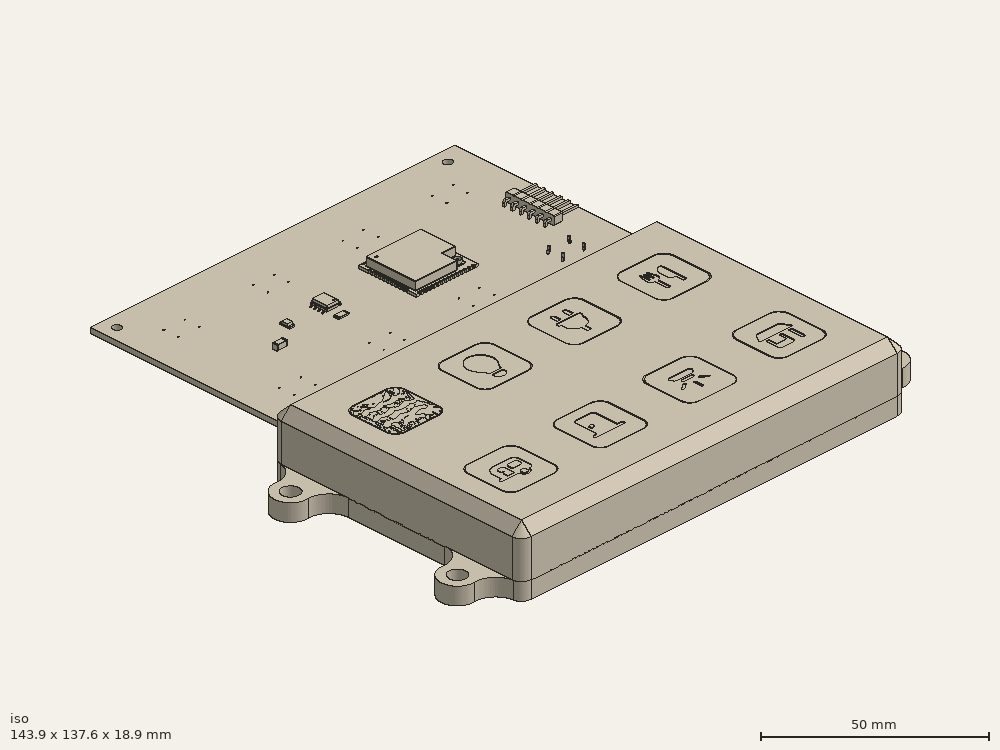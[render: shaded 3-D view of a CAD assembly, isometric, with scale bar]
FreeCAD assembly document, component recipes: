
FREECAD ASSEMBLY — COMPONENT RECIPES ("trailer-switch-panel-eight-buttons")

This assembly document has 11 components, labeled P0..P10 below (a component is one placed body or linked part). 10 of them carry a construction recipe — the FreeCAD feature program that regenerates the part from scratch, quoted from this document or its linked companion documents; the rest are supplied as boundary geometry only. No exploded tour is included for this assembly.
COMPONENT P0 — recipe-attached ("BodyButtonCap001", modeled in this document).
Construction recipe (the document's own serialized feature program — sketch geometry with constraints, then the solid features built on it; lengths are millimeters unless a unit is written):

FEATURE [Sketcher::SketchObject] Sketch036  label="SketchButtonCapBase"
  ArcFitTolerance = 1e-06
  AttachmentSupport = -> [XY_Plane014]
  ExternalTypes = [0]
  FullyConstrained = true
  MakeInternals = false
  MapMode = 5
  expr: Constraints[19] = <<VarSetButtonDimensions>>.Base_button_radius
  expr: Constraints[20] = <<VarSetButtonDimensions>>.Base_button_height
  expr: Constraints[21] = <<VarSetButtonDimensions>>.Base_button_width
  sketch-geometry (10):
    g0: LineSegment StartX=-5 StartY=-8 StartZ=0 EndX=5 EndY=-8 EndZ=0
    g1: LineSegment StartX=8 StartY=-5 StartZ=0 EndX=8 EndY=5 EndZ=0
    g2: LineSegment StartX=5 StartY=8 StartZ=0 EndX=-5 EndY=8 EndZ=0
    g3: LineSegment StartX=-8 StartY=5 StartZ=0 EndX=-8 EndY=-5 EndZ=0
    g4: ArcOfCircle CenterX=-5 CenterY=-5 CenterZ=0 NormalX=0 NormalY=0 NormalZ=1 AngleXU=0 Radius=3 StartAngle=3.14159 EndAngle=4.71239
    g5: ArcOfCircle CenterX=5 CenterY=-5 CenterZ=0 NormalX=0 NormalY=0 NormalZ=1 AngleXU=0 Radius=3 StartAngle=4.71239 EndAngle=6.28319
    g6: ArcOfCircle CenterX=5 CenterY=5 CenterZ=0 NormalX=0 NormalY=0 NormalZ=1 AngleXU=0 Radius=3 StartAngle=1e-16 EndAngle=1.5708
    g7: ArcOfCircle CenterX=-5 CenterY=5 CenterZ=0 NormalX=0 NormalY=0 NormalZ=1 AngleXU=0 Radius=3 StartAngle=1.5708 EndAngle=3.14159
    g8: GeomPoint [constr] X=8 Y=8 Z=0
    g9: GeomPoint [constr] X=0 Y=0 Z=0
  constraints (22):
    c: Tangent(g0,g4) = -1.5708
    c: Tangent(g0,g5) = -1.5708
    c: Tangent(g1,g5) = -1.5708
    c: Tangent(g1,g6) = -1.5708
    c: Tangent(g2,g6) = -1.5708
    c: Tangent(g2,g7) = -1.5708
    c: Tangent(g3,g7) = -1.5708
    c: Tangent(g3,g4) = -1.5708
    c: Horizontal(g0)
    c: Horizontal(g2)
    c: Vertical(g1)
    c: Vertical(g3)
    c: Equal(g4,g5)
    c: Equal(g5,g6)
    c: Equal(g6,g7)
    c: Symmetric(g2,g0,g9)
    c: PointOnObject(g8,g1)
    c: PointOnObject(g8,g2)
    c: Coincident(g9,g-1)
    c: Radius(g5) = 3
    c: DistanceY(g0,g2) = 16
    c: DistanceX(g3,g1) = 16
FEATURE [PartDesign::Plane] DatumPlane004
  AttachmentSupport = -> [Sketch036]
  Length = 60
  MapMode = 7
  Placement = pos=(8,-5,0) rot=(1,0,0;1.5708rad)
  ResizeMode = 0
  Width = 60
FEATURE [PartDesign::Pad] Pad026  label="PadButtonCapPlusBase"
  Direction = (0,0,1)
  Length = 4.59
  Length2 = 10
  Profile = -> Sketch036
  ReferenceAxis = -> Sketch036 [N_Axis]
  Refine = true
  SideType = 0
  Suppressed = false
  Type = 0
  Type2 = 0
  expr: Length = <<VarSetButtonDimensions>>.button_cap_height + <<VarSetButtonDimensions>>.Base_button_slide_depth + <<VarSetButtonDimensions>>.Base_base_thickness
FEATURE [PartDesign::Thickness] Thickness001  label="ThicknessCapWall"
  Base = -> Pad026 [Face9]
  BaseFeature = -> Pad026
  Intersection = false
  Join = 0
  Mode = 0
  Refine = true
  Reversed = true
  SupportTransform = false
  Suppressed = false
  Value = 1.5
  expr: Value = <<VarSetButtonDimensions>>.button_cap_wall_thickness
FEATURE [Sketcher::SketchObject] Sketch050  label="SketchButtonSkirt"
  ArcFitTolerance = 1e-06
  AttachmentSupport = -> [YZ_Plane014]
  ExternalGeometry = -> [Thickness001]
  ExternalTypes = [0]
  FullyConstrained = true
  MakeInternals = false
  MapMode = 5
  Placement = pos=(0,0,0) rot=(0.57735,0.57735,0.57735;2.0944rad)
  sketch-geometry (4):
    g0: LineSegment StartX=8 StartY=0 StartZ=0 EndX=8 EndY=2.5 EndZ=0
    g1: LineSegment StartX=8 StartY=2.5 StartZ=0 EndX=9 EndY=2.5 EndZ=0
    g2: LineSegment StartX=8 StartY=0 StartZ=0 EndX=9 EndY=0 EndZ=0
    g3: LineSegment StartX=9 StartY=2.5 StartZ=0 EndX=9 EndY=0 EndZ=0
  constraints (11):
    c: Coincident(g0,g-3)
    c: PointOnObject(g0,g-3)
    c: DistanceY(g0,g0) = 2.5
    c: Coincident(g1,g0)
    c: Horizontal(g1)
    c: Coincident(g2,g0)
    c: PointOnObject(g2,g-1)
    c: Coincident(g3,g1)
    c: Coincident(g3,g2)
    c: Vertical(g3)
    c: DistanceX(g1,g1) = 1
FEATURE [PartDesign::AdditivePipe] AdditivePipe  label="AdditivePipeButtonSkirt"
  AuxiliaryCurvilinear = true
  AuxiliarySpineTangent = false
  BaseFeature = -> Thickness001
  Binormal = (0,0,0)
  Mode = 0
  Profile = -> Sketch050
  Refine = true
  Spine = -> Thickness001 [Edge15,Edge18,Edge21,Edge23,Edge3,Edge6,Edge9,Edge12]
  SpineTangent = false
  Suppressed = false
  Transformation = 0
  Transition = 0
FEATURE [PartDesign::Pad] Pad035  label="PadButtonBottomContact"
  BaseFeature = -> AdditivePipe
  Direction = (0,0,-1)
  Length = 10
  Length2 = 10
  Profile = -> AdditivePipe [Face28]
  Refine = true
  SideType = 0
  Suppressed = false
  Type = 3
  Type2 = 0
  UpToFace = -> AdditivePipe [Face19]
FEATURE [PartDesign::Pocket] Pocket011  label="PocketBaseShorten"
  BaseFeature = -> Pad035
  Direction = (0,0,1)
  Length = 0.2
  Length2 = 5
  Profile = -> Pad035 [Face19]
  Refine = true
  SideType = 0
  Suppressed = false
  Type = 0
  Type2 = 0
FEATURE [PartDesign::Body] Body004  label="BodyButtonCapBlank"
  AllowCompound = false
  Group = -> [Sketch036,DatumPlane004,Pad026,Thickness001,Sketch050,AdditivePipe,Pad035,Pocket011]
  Origin = -> Origin014
  Placement = pos=(14.41,-15.25,1.6) rot=(0,0,1;0rad)
  Tip = -> Pocket011
COMPONENT P1 — same part as P0; its construction recipe is shown at P0.
COMPONENT P2 — same part as P0; its construction recipe is shown at P0.
COMPONENT P3 — same part as P0; its construction recipe is shown at P0.
COMPONENT P4 — same part as P0; its construction recipe is shown at P0.
COMPONENT P5 — same part as P0; its construction recipe is shown at P0.
COMPONENT P6 — same part as P0; its construction recipe is shown at P0.
COMPONENT P7 — same part as P0; its construction recipe is shown at P0.
COMPONENT P8 — recipe-attached ("BodyCaseBack001", modeled in this document).
Construction recipe (the document's own serialized feature program — sketch geometry with constraints, then the solid features built on it; lengths are millimeters unless a unit is written):

FEATURE [PartDesign::SubShapeBinder] Binder
  BindCopyOnChange = 0
  BindMode = 0
  ClaimChildren = false
  Context = -> Body [Binder.]
  Fuse = false
  MakeFace = true
  OffsetFill = false
  OffsetIntersection = false
  OffsetJoinType = 0
  OffsetOpenResult = false
  PartialLoad = false
  Refine = true
  Relative = true
  Support = -> [Body003[Pocket009.]]
  _Version = 2
FEATURE [Sketcher::SketchObject] Sketch  label="SketchBackOutline"
  ArcFitTolerance = 1e-06
  AttachmentSupport = -> [XY_Plane021]
  ExternalGeometry = -> [Binder]
  ExternalTypes = [0]
  FullyConstrained = true
  MakeInternals = false
  MapMode = 5
  sketch-geometry (8):
    g0: LineSegment StartX=116.87 StartY=6 StartZ=0 EndX=-3 EndY=6 EndZ=0
    g1: LineSegment StartX=-3 StartY=6 StartZ=0 EndX=-3 EndY=-71.81 EndZ=0
    g2: LineSegment StartX=-3 StartY=-71.81 StartZ=0 EndX=116.87 EndY=-71.81 EndZ=0
    g3: LineSegment StartX=116.87 StartY=-71.81 StartZ=0 EndX=116.87 EndY=6 EndZ=0
    g4: Circle CenterX=0 CenterY=-68.81 CenterZ=0 NormalX=0 NormalY=0 NormalZ=1 AngleXU=0 Radius=1.45
    g5: Circle CenterX=113.57 CenterY=-68.81 CenterZ=0 NormalX=0 NormalY=0 NormalZ=1 AngleXU=0 Radius=1.45
    g6: Circle CenterX=113.57 CenterY=2.7 CenterZ=0 NormalX=0 NormalY=0 NormalZ=1 AngleXU=0 Radius=1.45
    g7: Circle CenterX=0 CenterY=2.7 CenterZ=0 NormalX=0 NormalY=0 NormalZ=1 AngleXU=0 Radius=1.45
  constraints (18):
    c: Coincident(g0,g1)
    c: Coincident(g1,g2)
    c: Coincident(g2,g3)
    c: Coincident(g3,g0)
    c: Horizontal(g0)
    c: Horizontal(g2)
    c: Vertical(g1)
    c: Vertical(g3)
    c: Coincident(g0,g-4)
    c: Coincident(g1,g-6)
    c: Coincident(g5,g-7)
    c: Coincident(g6,g-8)
    c: Diameter(g4) = 2.9
    c: Equal(g4,g5)
    c: Coincident(g4,g-9)
    c: Coincident(g7,g-10)
    c: Equal(g7,g4)
    c: Equal(g4,g6)
FEATURE [PartDesign::Pad] Pad  label="PadCaseThickness"
  Direction = (0,0,1)
  Length = 5
  Length2 = 10
  Profile = -> Sketch
  ReferenceAxis = -> Sketch [N_Axis]
  Refine = true
  SideType = 0
  Suppressed = false
  Type = 0
  Type2 = 0
FEATURE [Sketcher::SketchObject] Sketch045  label="SketchMountingTabs"
  ArcFitTolerance = 1e-06
  AttachmentSupport = -> [Pad]
  ExternalGeometry = -> [Pad]
  ExternalTypes = [0]
  FullyConstrained = true
  MakeInternals = false
  MapMode = 5
  Placement = pos=(0,0,0) rot=(1,0,0;3.14159rad)
  sketch-geometry (24):
    g0: Circle CenterX=123.87 CenterY=58.84 CenterZ=0 NormalX=0 NormalY=0 NormalZ=1 AngleXU=0 Radius=2.5
    g1: Circle CenterX=-10 CenterY=58.84 CenterZ=0 NormalX=0 NormalY=0 NormalZ=1 AngleXU=0 Radius=2.5
    g2: Circle CenterX=-10 CenterY=6.97 CenterZ=0 NormalX=0 NormalY=0 NormalZ=1 AngleXU=0 Radius=2.5
    g3: Circle CenterX=123.87 CenterY=6.97 CenterZ=0 NormalX=0 NormalY=0 NormalZ=1 AngleXU=0 Radius=2.5
    g4: GeomPoint X=-3 Y=32.905 Z=0
    g5: GeomPoint X=116.87 Y=32.905 Z=0
    g6: GeomPoint X=-10 Y=32.905 Z=0
    g7: GeomPoint X=123.87 Y=32.905 Z=0
    g8: ArcOfCircle CenterX=-10 CenterY=58.84 CenterZ=0 NormalX=0 NormalY=0 NormalZ=1 AngleXU=0 Radius=5 StartAngle=1.48389 EndAngle=4.79929
    g9: ArcOfCircle CenterX=-10 CenterY=6.97 CenterZ=0 NormalX=0 NormalY=0 NormalZ=1 AngleXU=0 Radius=5 StartAngle=1.48389 EndAngle=4.79929
    g10: ArcOfCircle CenterX=123.87 CenterY=6.97 CenterZ=0 NormalX=0 NormalY=0 NormalZ=1 AngleXU=0 Radius=5 StartAngle=4.62549 EndAngle=7.94088
    g11: ArcOfCircle CenterX=123.87 CenterY=58.84 CenterZ=0 NormalX=0 NormalY=0 NormalZ=1 AngleXU=0 Radius=5 StartAngle=4.62549 EndAngle=7.94088
    g12: ArcOfCircle CenterX=122.912 CenterY=47.84 CenterZ=0 NormalX=0 NormalY=0 NormalZ=1 AngleXU=0 Radius=6.04167 StartAngle=1.48389 EndAngle=3.14159
    g13: ArcOfCircle CenterX=122.912 CenterY=69.84 CenterZ=0 NormalX=0 NormalY=0 NormalZ=1 AngleXU=0 Radius=6.04167 StartAngle=3.14159 EndAngle=4.79929
    g14: ArcOfCircle CenterX=122.912 CenterY=17.97 CenterZ=0 NormalX=0 NormalY=0 NormalZ=1 AngleXU=0 Radius=6.04167 StartAngle=3.14159 EndAngle=4.79929
    g15: ArcOfCircle CenterX=122.912 CenterY=-4.03 CenterZ=0 NormalX=0 NormalY=0 NormalZ=1 AngleXU=0 Radius=6.04167 StartAngle=1.48389 EndAngle=3.14159
    g16: ArcOfCircle CenterX=-9.04167 CenterY=-4.03 CenterZ=0 NormalX=0 NormalY=0 NormalZ=1 AngleXU=0 Radius=6.04167 StartAngle=0 EndAngle=1.6577
    g17: ArcOfCircle CenterX=-9.04167 CenterY=17.97 CenterZ=0 NormalX=0 NormalY=0 NormalZ=1 AngleXU=0 Radius=6.04167 StartAngle=4.62549 EndAngle=6.28319
    g18: ArcOfCircle CenterX=-9.04167 CenterY=47.84 CenterZ=0 NormalX=0 NormalY=0 NormalZ=1 AngleXU=0 Radius=6.04167 StartAngle=0 EndAngle=1.6577
    g19: ArcOfCircle CenterX=-9.04167 CenterY=69.84 CenterZ=0 NormalX=0 NormalY=0 NormalZ=1 AngleXU=0 Radius=6.04167 StartAngle=4.62549 EndAngle=6.28319
    g20: LineSegment StartX=-3 StartY=69.84 StartZ=0 EndX=-3 EndY=47.84 EndZ=0
    g21: LineSegment StartX=-3 StartY=17.97 StartZ=0 EndX=-3 EndY=-4.03 EndZ=0
    g22: LineSegment StartX=116.87 StartY=17.97 StartZ=0 EndX=116.87 EndY=-4.03 EndZ=0
    g23: LineSegment StartX=116.87 StartY=69.84 StartZ=0 EndX=116.87 EndY=47.84 EndZ=0
  constraints (58):
    c: Distance(g0,g-6) = 7
    c: Diameter(g0) = 5
    c: Equal(g0,g2)
    c: Equal(g2,g1)
    c: Horizontal(g1,g0)
    c: Equal(g0,g3)
    c: Vertical(g0,g3)
    c: Symmetric(g-5,g-5,g4)
    c: Symmetric(g-6,g-6,g5)
    c: Symmetric(g0,g3,g7)
    c: Symmetric(g1,g2,g6)
    c: Horizontal(g6,g4)
    c: Horizontal(g5,g7)
    c: Vertical(g2,g1)
    c: DistanceX(g1,g-5) = 7
    c: DistanceY(g-5,g-5) = 77.81
    c: DistanceY(g1,g-5) = 12.97
    c: PointOnObject(g15,g-6)
    c: PointOnObject(g16,g-5)
    c: Tangent(g19,g-5) = -1.5708
    c: Tangent(g19,g8) = 1.5708
    c: Tangent(g18,g8) = 1.5708
    c: Coincident(g8,g1)
    c: Vertical(g8,g8)
    c: DistanceY(g18,g19) = 22
    c: Radius(g8) = 5
    c: Tangent(g17,g-5) = -1.5708
    c: Tangent(g17,g9) = 1.5708
    c: Tangent(g16,g9) = 1.5708
    c: Equal(g9,g8)
    c: Coincident(g9,g2)
    c: DistanceY(g16,g17) = 22
    c: Vertical(g9,g9)
    c: Vertical(g9,g8)
    c: Tangent(g13,g-6) = -1.5708
    c: Tangent(g13,g11) = 1.5708
    c: Tangent(g12,g11) = 1.5708
    c: Tangent(g12,g-6) = -1.5708
    c: Coincident(g11,g0)
    c: Vertical(g11,g11)
    c: Equal(g8,g11)
    c: Horizontal(g13,g19)
    c: Tangent(g14,g-6) = -1.5708
    c: Tangent(g14,g10) = 1.5708
    c: Tangent(g15,g10) = 1.5708
    c: Vertical(g10,g10)
    c: Vertical(g10,g11)
    c: Coincident(g10,g3)
    c: Tangent(g-6,g15,g15) = -1.5708
    c: Horizontal(g14,g17)
    c: Tangent(g20,g19) = 1.5708
    c: Coincident(g20,g18)
    c: Coincident(g21,g17)
    c: Tangent(g21,g16) = 1.5708
    c: Coincident(g22,g14)
    c: Coincident(g22,g15)
    c: Coincident(g23,g13)
    c: Coincident(g23,g12)
FEATURE [PartDesign::Pad] Pad032  label="PadMountingTabs"
  BaseFeature = -> Pad
  Direction = (0,0,-1)
  Length = 5
  Length2 = 10
  Profile = -> Sketch045
  ReferenceAxis = -> Sketch045 [N_Axis]
  Refine = true
  Reversed = true
  SideType = 0
  Suppressed = false
  Type = 0
  Type2 = 0
FEATURE [Sketcher::SketchObject] Sketch046
  ArcFitTolerance = 1e-06
  AttachmentSupport = -> [Pad032]
  ExternalGeometry = -> [Pad032]
  ExternalTypes = [0]
  FullyConstrained = true
  MakeInternals = false
  MapMode = 5
  Placement = pos=(0,0,0) rot=(1,0,0;3.14159rad)
  sketch-geometry (4):
    g0: Circle CenterX=0 CenterY=-2.7 CenterZ=0 NormalX=0 NormalY=0 NormalZ=1 AngleXU=0 Radius=2.3
    g1: Circle CenterX=113.57 CenterY=-2.7 CenterZ=0 NormalX=0 NormalY=0 NormalZ=1 AngleXU=0 Radius=2.3
    g2: Circle CenterX=113.57 CenterY=68.81 CenterZ=0 NormalX=0 NormalY=0 NormalZ=1 AngleXU=0 Radius=2.3
    g3: Circle CenterX=0 CenterY=68.81 CenterZ=0 NormalX=0 NormalY=0 NormalZ=1 AngleXU=0 Radius=2.3
  constraints (8):
    c: Coincident(g1,g-4)
    c: Coincident(g2,g-3)
    c: Diameter(g3) = 4.6
    c: Equal(g3,g2)
    c: Equal(g2,g1)
    c: Equal(g1,g0)
    c: Coincident(g3,g-5)
    c: Coincident(g-6,g0)
FEATURE [PartDesign::Pocket] Pocket
  BaseFeature = -> Pad032
  Direction = (0,0,1)
  Length = 3.5
  Length2 = 5
  Profile = -> Sketch046
  ReferenceAxis = -> Sketch046 [N_Axis]
  Refine = true
  SideType = 0
  Suppressed = false
  Type = 0
  Type2 = 0
FEATURE [Sketcher::SketchObject] Sketch051
  ArcFitTolerance = 1e-06
  AttachmentSupport = -> [Pocket]
  ExternalGeometry = -> [Pocket]
  ExternalTypes = [0]
  FullyConstrained = true
  MakeInternals = false
  MapMode = 5
  Placement = pos=(0,0,5) rot=(0,0,1;0rad)
  sketch-geometry (6):
    g0: GeomPoint X=56.935 Y=-32.905 Z=0
    g1: LineSegment StartX=7 StartY=1 StartZ=0 EndX=7 EndY=-66.81 EndZ=0
    g2: LineSegment StartX=7 StartY=-66.81 StartZ=0 EndX=106.87 EndY=-66.81 EndZ=0
    g3: LineSegment StartX=106.87 StartY=-66.81 StartZ=0 EndX=106.87 EndY=1 EndZ=0
    g4: LineSegment StartX=106.87 StartY=1 StartZ=0 EndX=7 EndY=1 EndZ=0
    g5: GeomPoint [constr] X=56.935 Y=-32.905 Z=0
  constraints (13):
    c: Symmetric(g-3,g-4,g0)
    c: Coincident(g1,g2)
    c: Coincident(g2,g3)
    c: Coincident(g3,g4)
    c: Coincident(g4,g1)
    c: Vertical(g1)
    c: Vertical(g3)
    c: Horizontal(g2)
    c: Horizontal(g4)
    c: Symmetric(g3,g1,g5)
    c: Coincident(g5,g0)
    c: DistanceY(g1,g-3) = 5
    c: DistanceX(g-3,g1) = 10
FEATURE [PartDesign::Pocket] Pocket012
  BaseFeature = -> Pocket
  Direction = (0,0,-1)
  Length = 2
  Length2 = 5
  Profile = -> Sketch051
  ReferenceAxis = -> Sketch051 [N_Axis]
  Refine = true
  SideType = 0
  Suppressed = false
  Type = 0
  Type2 = 0
FEATURE [PartDesign::Fillet] Fillet001
  Base = -> Pocket012 [Edge32,Edge2,Edge66,Edge65]
  BaseFeature = -> Pocket012
  Radius = 3
  Refine = true
  SupportTransform = false
  Suppressed = false
  UseAllEdges = false
FEATURE [PartDesign::Body] Body  label="BodyCaseBack"
  AllowCompound = false
  Group = -> [Binder,Sketch,Pad,Sketch045,Pad032,Sketch046,Pocket,Sketch051,Pocket012,Fillet001]
  Origin = -> Origin021
  Placement = pos=(0,0,-12.73) rot=(0,0,1;0rad)
  Tip = -> Fillet001
COMPONENT P9 — recipe-attached ("BodyFrontMountPcbButtonCover001", modeled in this document).
Construction recipe (the document's own serialized feature program — sketch geometry with constraints, then the solid features built on it; lengths are millimeters unless a unit is written):

FEATURE [PartDesign::SubShapeBinder] Binder006  label="BinderPcb001"
  BindCopyOnChange = 0
  BindMode = 0
  ClaimChildren = false
  Context = -> Body003 [Binder006.]
  Fuse = false
  MakeFace = true
  OffsetFill = false
  OffsetIntersection = false
  OffsetJoinType = 0
  OffsetOpenResult = false
  PartialLoad = false
  Placement = pos=(0,0,-3.64) rot=(0,0,1;0rad)
  Refine = true
  Relative = true
  Support = -> [Board_cc27]
  _Version = 2
FEATURE [Sketcher::SketchObject] Sketch033  label="SketchBackPlateToCover"
  ArcFitTolerance = 1e-06
  AttachmentSupport = -> [XY_Plane013]
  ExternalGeometry = -> [Binder006]
  ExternalTypes = [0]
  FullyConstrained = true
  MakeInternals = false
  MapMode = 5
  expr: Constraints[19] = <<VarSetButtonDimensions>>.Base_button_width + <<VarSetButtonDimensions>>.tolerance
  expr: Constraints[20] = <<VarSetButtonDimensions>>.Base_button_height + <<VarSetButtonDimensions>>.tolerance
  expr: Constraints[33] = <<VarSetButtonDimensions>>.Base_button_radius
  sketch-geometry (84):
    g0: LineSegment StartX=6.2 StartY=-10.05 StartZ=0 EndX=6.2 EndY=-20.45 EndZ=0
    g1: LineSegment StartX=9.2 StartY=-23.45 StartZ=0 EndX=19.6 EndY=-23.45 EndZ=0
    g2: LineSegment StartX=22.6 StartY=-20.45 StartZ=0 EndX=22.6 EndY=-10.05 EndZ=0
    g3: LineSegment StartX=19.6 StartY=-7.05 StartZ=0 EndX=9.2 EndY=-7.05 EndZ=0
    g4: ArcOfCircle CenterX=9.2 CenterY=-10.05 CenterZ=0 NormalX=0 NormalY=0 NormalZ=1 AngleXU=0 Radius=3 StartAngle=1.5708 EndAngle=3.14159
    g5: ArcOfCircle CenterX=9.2 CenterY=-20.45 CenterZ=0 NormalX=0 NormalY=0 NormalZ=1 AngleXU=0 Radius=3 StartAngle=3.14159 EndAngle=4.71239
    g6: ArcOfCircle CenterX=19.6 CenterY=-20.45 CenterZ=0 NormalX=0 NormalY=0 NormalZ=1 AngleXU=0 Radius=3 StartAngle=4.71239 EndAngle=6.28319
    g7: ArcOfCircle CenterX=19.6 CenterY=-10.05 CenterZ=0 NormalX=0 NormalY=0 NormalZ=1 AngleXU=0 Radius=3 StartAngle=6e-16 EndAngle=1.5708
    g8: GeomPoint [constr] X=6.2 Y=-7.05 Z=0
    g9: GeomPoint [constr] X=22.6 Y=-23.45 Z=0
    g10: LineSegment StartX=-3 StartY=6 StartZ=0 EndX=-3 EndY=-71.81 EndZ=0
    g11: LineSegment StartX=-3 StartY=-71.81 StartZ=0 EndX=116.87 EndY=-71.81 EndZ=0
    g12: LineSegment StartX=116.87 StartY=-71.81 StartZ=0 EndX=116.87 EndY=6 EndZ=0
    g13: LineSegment StartX=116.87 StartY=6 StartZ=0 EndX=-3 EndY=6 EndZ=0
    g14: LineSegment StartX=34.04 StartY=-10.05 StartZ=0 EndX=34.04 EndY=-20.45 EndZ=0
    g15: LineSegment StartX=37.04 StartY=-23.45 StartZ=0 EndX=47.44 EndY=-23.45 EndZ=0
    g16: LineSegment StartX=50.44 StartY=-20.45 StartZ=0 EndX=50.44 EndY=-10.05 EndZ=0
    g17: LineSegment StartX=47.44 StartY=-7.05 StartZ=0 EndX=37.04 EndY=-7.05 EndZ=0
    g18: ArcOfCircle CenterX=37.04 CenterY=-10.05 CenterZ=0 NormalX=0 NormalY=0 NormalZ=1 AngleXU=0 Radius=3 StartAngle=1.5708 EndAngle=3.14159
    g19: ArcOfCircle CenterX=37.04 CenterY=-20.45 CenterZ=0 NormalX=0 NormalY=0 NormalZ=1 AngleXU=0 Radius=3 StartAngle=3.14159 EndAngle=4.71239
    g20: ArcOfCircle CenterX=47.44 CenterY=-20.45 CenterZ=0 NormalX=0 NormalY=0 NormalZ=1 AngleXU=0 Radius=3 StartAngle=4.71239 EndAngle=6.28319
    g21: ArcOfCircle CenterX=47.44 CenterY=-10.05 CenterZ=0 NormalX=0 NormalY=0 NormalZ=1 AngleXU=0 Radius=3 StartAngle=0 EndAngle=1.5708
    g22: GeomPoint [constr] X=50.44 Y=-23.45 Z=0
    g23: GeomPoint [constr] X=42.24 Y=-15.25 Z=0
    g24: LineSegment StartX=61.88 StartY=-10.05 StartZ=0 EndX=61.88 EndY=-20.45 EndZ=0
    g25: LineSegment StartX=64.88 StartY=-23.45 StartZ=0 EndX=75.28 EndY=-23.45 EndZ=0
    g26: LineSegment StartX=78.28 StartY=-20.45 StartZ=0 EndX=78.28 EndY=-10.05 EndZ=0
    g27: LineSegment StartX=75.28 StartY=-7.05 StartZ=0 EndX=64.88 EndY=-7.05 EndZ=0
    g28: ArcOfCircle CenterX=64.88 CenterY=-10.05 CenterZ=0 NormalX=0 NormalY=0 NormalZ=1 AngleXU=0 Radius=3 StartAngle=1.5708 EndAngle=3.14159
    g29: ArcOfCircle CenterX=64.88 CenterY=-20.45 CenterZ=0 NormalX=0 NormalY=0 NormalZ=1 AngleXU=0 Radius=3 StartAngle=3.14159 EndAngle=4.71239
    g30: ArcOfCircle CenterX=75.28 CenterY=-20.45 CenterZ=0 NormalX=0 NormalY=0 NormalZ=1 AngleXU=0 Radius=3 StartAngle=4.71239 EndAngle=6.28319
    g31: ArcOfCircle CenterX=75.28 CenterY=-10.05 CenterZ=0 NormalX=0 NormalY=0 NormalZ=1 AngleXU=0 Radius=3 StartAngle=1e-16 EndAngle=1.5708
    g32: GeomPoint [constr] X=78.28 Y=-23.45 Z=0
    g33: GeomPoint [constr] X=70.08 Y=-15.25 Z=0
    g34: LineSegment StartX=89.72 StartY=-10.05 StartZ=0 EndX=89.72 EndY=-20.45 EndZ=0
    g35: LineSegment StartX=92.72 StartY=-23.45 StartZ=0 EndX=103.12 EndY=-23.45 EndZ=0
    g36: LineSegment StartX=106.12 StartY=-20.45 StartZ=0 EndX=106.12 EndY=-10.05 EndZ=0
    g37: LineSegment StartX=103.12 StartY=-7.05 StartZ=0 EndX=92.72 EndY=-7.05 EndZ=0
    g38: ArcOfCircle CenterX=92.72 CenterY=-10.05 CenterZ=0 NormalX=0 NormalY=0 NormalZ=1 AngleXU=0 Radius=3 StartAngle=1.5708 EndAngle=3.14159
    g39: ArcOfCircle CenterX=92.72 CenterY=-20.45 CenterZ=0 NormalX=0 NormalY=0 NormalZ=1 AngleXU=0 Radius=3 StartAngle=3.14159 EndAngle=4.71239
    g40: ArcOfCircle CenterX=103.12 CenterY=-20.45 CenterZ=0 NormalX=0 NormalY=0 NormalZ=1 AngleXU=0 Radius=3 StartAngle=4.71239 EndAngle=6.28319
    g41: ArcOfCircle CenterX=103.12 CenterY=-10.05 CenterZ=0 NormalX=0 NormalY=0 NormalZ=1 AngleXU=0 Radius=3 StartAngle=3e-16 EndAngle=1.5708
    g42: GeomPoint [constr] X=106.12 Y=-23.45 Z=0
    g43: GeomPoint [constr] X=97.92 Y=-15.25 Z=0
    g44: LineSegment StartX=6 StartY=-46.08 StartZ=0 EndX=6 EndY=-56.48 EndZ=0
    g45: LineSegment StartX=9 StartY=-59.48 StartZ=0 EndX=19.4 EndY=-59.48 EndZ=0
    g46: LineSegment StartX=22.4 StartY=-56.48 StartZ=0 EndX=22.4 EndY=-46.08 EndZ=0
    g47: LineSegment StartX=19.4 StartY=-43.08 StartZ=0 EndX=9 EndY=-43.08 EndZ=0
    g48: ArcOfCircle CenterX=9 CenterY=-46.08 CenterZ=0 NormalX=0 NormalY=0 NormalZ=1 AngleXU=0 Radius=3 StartAngle=1.5708 EndAngle=3.14159
    g49: ArcOfCircle CenterX=9 CenterY=-56.48 CenterZ=0 NormalX=0 NormalY=0 NormalZ=1 AngleXU=0 Radius=3 StartAngle=3.14159 EndAngle=4.71239
    g50: ArcOfCircle CenterX=19.4 CenterY=-56.48 CenterZ=0 NormalX=0 NormalY=0 NormalZ=1 AngleXU=0 Radius=3 StartAngle=4.71239 EndAngle=6.28319
    g51: ArcOfCircle CenterX=19.4 CenterY=-46.08 CenterZ=0 NormalX=0 NormalY=0 NormalZ=1 AngleXU=0 Radius=3 StartAngle=9e-16 EndAngle=1.5708
    g52: GeomPoint [constr] X=22.4 Y=-59.48 Z=0
    g53: GeomPoint [constr] X=14.2 Y=-51.28 Z=0
    g54: LineSegment StartX=33.84 StartY=-46.08 StartZ=0 EndX=33.84 EndY=-56.48 EndZ=0
    g55: LineSegment StartX=36.84 StartY=-59.48 StartZ=0 EndX=47.24 EndY=-59.48 EndZ=0
    g56: LineSegment StartX=50.24 StartY=-56.48 StartZ=0 EndX=50.24 EndY=-46.08 EndZ=0
    g57: LineSegment StartX=47.24 StartY=-43.08 StartZ=0 EndX=36.84 EndY=-43.08 EndZ=0
    g58: ArcOfCircle CenterX=36.84 CenterY=-46.08 CenterZ=0 NormalX=0 NormalY=0 NormalZ=1 AngleXU=0 Radius=3 StartAngle=1.5708 EndAngle=3.14159
    g59: ArcOfCircle CenterX=36.84 CenterY=-56.48 CenterZ=0 NormalX=0 NormalY=0 NormalZ=1 AngleXU=0 Radius=3 StartAngle=3.14159 EndAngle=4.71239
    g60: ArcOfCircle CenterX=47.24 CenterY=-56.48 CenterZ=0 NormalX=0 NormalY=0 NormalZ=1 AngleXU=0 Radius=3 StartAngle=4.71239 EndAngle=6.28319
    g61: ArcOfCircle CenterX=47.24 CenterY=-46.08 CenterZ=0 NormalX=0 NormalY=0 NormalZ=1 AngleXU=0 Radius=3 StartAngle=7e-16 EndAngle=1.5708
    g62: GeomPoint [constr] X=50.24 Y=-59.48 Z=0
    g63: GeomPoint [constr] X=42.04 Y=-51.28 Z=0
    g64: LineSegment StartX=61.68 StartY=-46.08 StartZ=0 EndX=61.68 EndY=-56.48 EndZ=0
    g65: LineSegment StartX=64.68 StartY=-59.48 StartZ=0 EndX=75.08 EndY=-59.48 EndZ=0
    g66: LineSegment StartX=78.08 StartY=-56.48 StartZ=0 EndX=78.08 EndY=-46.08 EndZ=0
    g67: LineSegment StartX=75.08 StartY=-43.08 StartZ=0 EndX=64.68 EndY=-43.08 EndZ=0
    g68: ArcOfCircle CenterX=64.68 CenterY=-46.08 CenterZ=0 NormalX=0 NormalY=0 NormalZ=1 AngleXU=0 Radius=3 StartAngle=1.5708 EndAngle=3.14159
    g69: ArcOfCircle CenterX=64.68 CenterY=-56.48 CenterZ=0 NormalX=0 NormalY=0 NormalZ=1 AngleXU=0 Radius=3 StartAngle=3.14159 EndAngle=4.71239
    g70: ArcOfCircle CenterX=75.08 CenterY=-56.48 CenterZ=0 NormalX=0 NormalY=0 NormalZ=1 AngleXU=0 Radius=3 StartAngle=4.71239 EndAngle=6.28319
    g71: ArcOfCircle CenterX=75.08 CenterY=-46.08 CenterZ=0 NormalX=0 NormalY=0 NormalZ=1 AngleXU=0 Radius=3 StartAngle=9e-16 EndAngle=1.5708
    g72: GeomPoint [constr] X=78.08 Y=-59.48 Z=0
    g73: GeomPoint [constr] X=69.88 Y=-51.28 Z=0
    g74: LineSegment StartX=89.52 StartY=-46.08 StartZ=0 EndX=89.52 EndY=-56.48 EndZ=0
    g75: LineSegment StartX=92.52 StartY=-59.48 StartZ=0 EndX=102.92 EndY=-59.48 EndZ=0
    g76: LineSegment StartX=105.92 StartY=-56.48 StartZ=0 EndX=105.92 EndY=-46.08 EndZ=0
    g77: LineSegment StartX=102.92 StartY=-43.08 StartZ=0 EndX=92.52 EndY=-43.08 EndZ=0
    g78: ArcOfCircle CenterX=92.52 CenterY=-46.08 CenterZ=0 NormalX=0 NormalY=0 NormalZ=1 AngleXU=0 Radius=3 StartAngle=1.5708 EndAngle=3.14159
    g79: ArcOfCircle CenterX=92.52 CenterY=-56.48 CenterZ=0 NormalX=0 NormalY=0 NormalZ=1 AngleXU=0 Radius=3 StartAngle=3.14159 EndAngle=4.71239
    g80: ArcOfCircle CenterX=102.92 CenterY=-56.48 CenterZ=0 NormalX=0 NormalY=0 NormalZ=1 AngleXU=0 Radius=3 StartAngle=4.71239 EndAngle=6.28319
    g81: ArcOfCircle CenterX=102.92 CenterY=-46.08 CenterZ=0 NormalX=0 NormalY=0 NormalZ=1 AngleXU=0 Radius=3 StartAngle=6e-16 EndAngle=1.5708
    g82: GeomPoint [constr] X=105.92 Y=-59.48 Z=0
    g83: GeomPoint [constr] X=97.72 Y=-51.28 Z=0
  constraints (189):
    c: Tangent(g0,g4) = -1.5708
    c: Tangent(g0,g5) = -1.5708
    c: Tangent(g1,g5) = -1.5708
    c: Tangent(g1,g6) = -1.5708
    c: Tangent(g2,g6) = -1.5708
    c: Tangent(g2,g7) = -1.5708
    c: Tangent(g3,g7) = -1.5708
    c: Tangent(g3,g4) = -1.5708
    c: Vertical(g0)
    c: Vertical(g2)
    c: Horizontal(g1)
    c: Horizontal(g3)
    c: Equal(g4,g5)
    c: Equal(g5,g6)
    c: Equal(g6,g7)
    c: PointOnObject(g8,g0)
    c: PointOnObject(g8,g3)
    c: PointOnObject(g9,g1)
    c: PointOnObject(g9,g2)
    c: Distance(g0,g2) = 16.4
    c: Distance(g1,g3) = 16.4
    c: Coincident(g10,g11)
    c: Coincident(g11,g12)
    c: Coincident(g12,g13)
    c: Coincident(g13,g10)
    c: Vertical(g10)
    c: Vertical(g12)
    c: Horizontal(g11)
    c: Horizontal(g13)
    c: DistanceX(g10,g-1) = 3
    c: DistanceY(g-1,g10) = 6
    c: DistanceX(g-5,g11) = 3
    c: DistanceY(g11,g-5) = 6
    c: Radius(g7) = 3
    c: Symmetric(g4,g6,g-7)
    c: Tangent(g14,g18) = -1.5708
    c: Tangent(g14,g19) = -1.5708
    c: Tangent(g15,g19) = -1.5708
    c: Tangent(g15,g20) = -1.5708
    c: Tangent(g16,g20) = -1.5708
    c: Tangent(g16,g21) = -1.5708
    c: Tangent(g17,g21) = -1.5708
    c: Tangent(g17,g18) = -1.5708
    c: Vertical(g14)
    c: Vertical(g16)
    c: Horizontal(g15)
    c: Horizontal(g17)
    c: Equal(g18,g19)
    c: Equal(g19,g20)
    c: Equal(g20,g21)
    c: Symmetric(g16,g14,g23)
    c: PointOnObject(g22,g15)
    c: PointOnObject(g22,g16)
    c: Coincident(g23,g-8)
    c: Tangent(g24,g28) = -1.5708
    c: Tangent(g24,g29) = -1.5708
    c: Tangent(g25,g29) = -1.5708
    c: Tangent(g25,g30) = -1.5708
    c: Tangent(g26,g30) = -1.5708
    c: Tangent(g26,g31) = -1.5708
    c: Tangent(g27,g31) = -1.5708
    c: Tangent(g27,g28) = -1.5708
    c: Vertical(g24)
    c: Vertical(g26)
    c: Horizontal(g25)
    c: Horizontal(g27)
    c: Equal(g28,g29)
    c: Equal(g29,g30)
    c: Equal(g30,g31)
    c: Symmetric(g26,g24,g33)
    c: PointOnObject(g32,g25)
    c: PointOnObject(g32,g26)
    c: Coincident(g33,g-9)
    c: Tangent(g34,g38) = -1.5708
    c: Tangent(g34,g39) = -1.5708
    c: Tangent(g35,g39) = -1.5708
    c: Tangent(g35,g40) = -1.5708
    c: Tangent(g36,g40) = -1.5708
    c: Tangent(g36,g41) = -1.5708
    c: Tangent(g37,g41) = -1.5708
    c: Tangent(g37,g38) = -1.5708
    c: Vertical(g34)
    c: Vertical(g36)
    c: Horizontal(g35)
    c: Horizontal(g37)
    c: Equal(g38,g39)
    c: Equal(g39,g40)
    c: Equal(g40,g41)
    c: Symmetric(g36,g34,g43)
    c: PointOnObject(g42,g35)
    c: PointOnObject(g42,g36)
    c: Coincident(g43,g-10)
    c: Tangent(g44,g48) = -1.5708
    c: Tangent(g44,g49) = -1.5708
    c: Tangent(g45,g49) = -1.5708
    c: Tangent(g45,g50) = -1.5708
    c: Tangent(g46,g50) = -1.5708
    c: Tangent(g46,g51) = -1.5708
    c: Tangent(g47,g51) = -1.5708
    c: Tangent(g47,g48) = -1.5708
    c: Vertical(g44)
    c: Vertical(g46)
    c: Horizontal(g45)
    c: Horizontal(g47)
    c: Equal(g48,g49)
    c: Equal(g49,g50)
    c: Equal(g50,g51)
    c: Symmetric(g46,g44,g53)
    c: PointOnObject(g52,g45)
    c: PointOnObject(g52,g46)
    c: Coincident(g53,g-14)
    c: Tangent(g54,g58) = -1.5708
    c: Tangent(g54,g59) = -1.5708
    c: Tangent(g55,g59) = -1.5708
    c: Tangent(g55,g60) = -1.5708
    c: Tangent(g56,g60) = -1.5708
    c: Tangent(g56,g61) = -1.5708
    c: Tangent(g57,g61) = -1.5708
    c: Tangent(g57,g58) = -1.5708
    c: Vertical(g54)
    c: Vertical(g56)
    c: Horizontal(g55)
    c: Horizontal(g57)
    c: Equal(g58,g59)
    c: Equal(g59,g60)
    c: Equal(g60,g61)
    c: Symmetric(g56,g54,g63)
    c: PointOnObject(g62,g55)
    c: PointOnObject(g62,g56)
    c: Coincident(g63,g-13)
    c: Tangent(g64,g68) = -1.5708
    c: Tangent(g64,g69) = -1.5708
    c: Tangent(g65,g69) = -1.5708
    c: Tangent(g65,g70) = -1.5708
    c: Tangent(g66,g70) = -1.5708
    c: Tangent(g66,g71) = -1.5708
    c: Tangent(g67,g71) = -1.5708
    c: Tangent(g67,g68) = -1.5708
    c: Vertical(g64)
    c: Vertical(g66)
    c: Horizontal(g65)
    c: Horizontal(g67)
    c: Equal(g68,g69)
    c: Equal(g69,g70)
    c: Equal(g70,g71)
    c: Symmetric(g66,g64,g73)
    c: PointOnObject(g72,g65)
    c: PointOnObject(g72,g66)
    c: Coincident(g73,g-12)
    c: Tangent(g74,g78) = -1.5708
    c: Tangent(g74,g79) = -1.5708
    c: Tangent(g75,g79) = -1.5708
    c: Tangent(g75,g80) = -1.5708
    c: Tangent(g76,g80) = -1.5708
    c: Tangent(g76,g81) = -1.5708
    c: Tangent(g77,g81) = -1.5708
    c: Tangent(g77,g78) = -1.5708
    c: Vertical(g74)
    c: Vertical(g76)
    c: Horizontal(g75)
    c: Horizontal(g77)
    c: Equal(g78,g79)
    c: Equal(g79,g80)
    c: Equal(g80,g81)
    c: Symmetric(g76,g74,g83)
    c: PointOnObject(g82,g75)
    c: PointOnObject(g82,g76)
    c: Coincident(g83,g-11)
    c: Equal(g4,g18)
    c: Equal(g18,g48)
    c: Equal(g48,g58)
    c: Equal(g58,g68)
    c: Equal(g68,g28)
    c: Equal(g28,g38)
    c: Equal(g38,g78)
    c: Equal(g2,g16)
    c: Equal(g16,g26)
    c: Equal(g26,g36)
    c: Equal(g36,g76)
    c: Equal(g76,g66)
    c: Equal(g66,g56)
    c: Equal(g56,g46)
    c: Equal(g3,g17)
    c: Equal(g17,g27)
    c: Equal(g27,g37)
    c: Equal(g37,g77)
    c: Equal(g77,g67)
    c: Equal(g67,g57)
    c: Equal(g57,g47)
FEATURE [PartDesign::Pad] Pad024  label="PadOuterWalls"
  Direction = (0,0,1)
  Length = 1.5
  Length2 = 10
  Profile = -> Sketch033
  ReferenceAxis = -> Sketch033 [N_Axis]
  Refine = true
  SideType = 0
  Suppressed = false
  Type = 0
  Type2 = 0
  expr: Length = <<VarSetButtonDimensions>>.Base_base_thickness
FEATURE [Sketcher::SketchObject] Sketch034  label="SketchButtonSlide"
  ArcFitTolerance = 1e-06
  AttachmentSupport = -> [Pad024]
  ExternalGeometry = -> [Pad024]
  ExternalTypes = [0]
  FullyConstrained = true
  MakeInternals = false
  MapMode = 5
  Placement = pos=(0,0,1.5) rot=(0,0,1;0rad)
  expr: Constraints[29] = <<VarSetButtonDimensions>>.Base_button_radius
  expr: Constraints[30] = <<VarSetButtonDimensions>>.Base_button_width + <<VarSetButtonDimensions>>.tolerance + <<VarSetButtonDimensions>>.button_snap_thickness * 2 + <<VarSetButtonDimensions>>.button_tab_depth
  expr: Constraints[31] = <<VarSetButtonDimensions>>.Base_button_width + <<VarSetButtonDimensions>>.tolerance + <<VarSetButtonDimensions>>.button_snap_thickness * 2 + <<VarSetButtonDimensions>>.button_tab_depth
  sketch-geometry (93):
    g0: LineSegment StartX=-3 StartY=6 StartZ=0 EndX=-3 EndY=-71.81 EndZ=0
    g1: LineSegment StartX=-3 StartY=-71.81 StartZ=0 EndX=116.87 EndY=-71.81 EndZ=0
    g2: LineSegment StartX=116.87 StartY=-71.81 StartZ=0 EndX=116.87 EndY=6 EndZ=0
    g3: LineSegment StartX=116.87 StartY=6 StartZ=0 EndX=-3 EndY=6 EndZ=0
    g4: LineSegment StartX=5.2 StartY=-9.05 StartZ=0 EndX=5.2 EndY=-21.45 EndZ=0
    g5: LineSegment StartX=8.2 StartY=-24.45 StartZ=0 EndX=20.6 EndY=-24.45 EndZ=0
    g6: LineSegment StartX=23.6 StartY=-21.45 StartZ=0 EndX=23.6 EndY=-9.05 EndZ=0
    g7: LineSegment StartX=20.6 StartY=-6.05 StartZ=0 EndX=8.2 EndY=-6.05 EndZ=0
    g8: ArcOfCircle CenterX=8.2 CenterY=-9.05 CenterZ=0 NormalX=0 NormalY=0 NormalZ=1 AngleXU=0 Radius=3 StartAngle=1.5708 EndAngle=3.14159
    g9: ArcOfCircle CenterX=8.2 CenterY=-21.45 CenterZ=0 NormalX=0 NormalY=0 NormalZ=1 AngleXU=0 Radius=3 StartAngle=3.14159 EndAngle=4.71239
    g10: ArcOfCircle CenterX=20.6 CenterY=-21.45 CenterZ=0 NormalX=0 NormalY=0 NormalZ=1 AngleXU=0 Radius=3 StartAngle=4.71239 EndAngle=6.28319
    g11: ArcOfCircle CenterX=20.6 CenterY=-9.05 CenterZ=0 NormalX=0 NormalY=0 NormalZ=1 AngleXU=0 Radius=3 StartAngle=0 EndAngle=1.5708
    g12: GeomPoint [constr] X=5.2 Y=-6.05 Z=0
    g13: GeomPoint [constr] X=23.6 Y=-24.45 Z=0
    g14: GeomPoint X=14.4 Y=-15.25 Z=0
    g15: GeomPoint X=14.4 Y=-15.25 Z=0
    g16: LineSegment StartX=33.04 StartY=-9.05 StartZ=0 EndX=33.04 EndY=-21.45 EndZ=0
    g17: LineSegment StartX=36.04 StartY=-24.45 StartZ=0 EndX=48.44 EndY=-24.45 EndZ=0
    g18: LineSegment StartX=51.44 StartY=-21.45 StartZ=0 EndX=51.44 EndY=-9.05 EndZ=0
    g19: LineSegment StartX=48.44 StartY=-6.05 StartZ=0 EndX=36.04 EndY=-6.05 EndZ=0
    g20: ArcOfCircle CenterX=36.04 CenterY=-9.05 CenterZ=0 NormalX=0 NormalY=0 NormalZ=1 AngleXU=0 Radius=3 StartAngle=1.5708 EndAngle=3.14159
    g21: ArcOfCircle CenterX=36.04 CenterY=-21.45 CenterZ=0 NormalX=0 NormalY=0 NormalZ=1 AngleXU=0 Radius=3 StartAngle=3.14159 EndAngle=4.71239
    g22: ArcOfCircle CenterX=48.44 CenterY=-21.45 CenterZ=0 NormalX=0 NormalY=0 NormalZ=1 AngleXU=0 Radius=3 StartAngle=4.71239 EndAngle=6.28319
    g23: ArcOfCircle CenterX=48.44 CenterY=-9.05 CenterZ=0 NormalX=0 NormalY=0 NormalZ=1 AngleXU=0 Radius=3 StartAngle=0 EndAngle=1.5708
    g24: GeomPoint [constr] X=33.04 Y=-6.05 Z=0
    g25: GeomPoint [constr] X=51.44 Y=-24.45 Z=0
    g26: LineSegment StartX=60.88 StartY=-9.05 StartZ=0 EndX=60.88 EndY=-21.45 EndZ=0
    g27: LineSegment StartX=63.88 StartY=-24.45 StartZ=0 EndX=76.28 EndY=-24.45 EndZ=0
    g28: LineSegment StartX=79.28 StartY=-21.45 StartZ=0 EndX=79.28 EndY=-9.05 EndZ=0
    g29: LineSegment StartX=76.28 StartY=-6.05 StartZ=0 EndX=63.88 EndY=-6.05 EndZ=0
    g30: ArcOfCircle CenterX=63.88 CenterY=-9.05 CenterZ=0 NormalX=0 NormalY=0 NormalZ=1 AngleXU=0 Radius=3 StartAngle=1.5708 EndAngle=3.14159
    g31: ArcOfCircle CenterX=63.88 CenterY=-21.45 CenterZ=0 NormalX=0 NormalY=0 NormalZ=1 AngleXU=0 Radius=3 StartAngle=3.14159 EndAngle=4.71239
    g32: ArcOfCircle CenterX=76.28 CenterY=-21.45 CenterZ=0 NormalX=0 NormalY=0 NormalZ=1 AngleXU=0 Radius=3 StartAngle=4.71239 EndAngle=6.28319
    g33: ArcOfCircle CenterX=76.28 CenterY=-9.05 CenterZ=0 NormalX=0 NormalY=0 NormalZ=1 AngleXU=0 Radius=3 StartAngle=0 EndAngle=1.5708
    g34: GeomPoint [constr] X=60.88 Y=-6.05 Z=0
    g35: GeomPoint [constr] X=79.28 Y=-24.45 Z=0
    g36: LineSegment StartX=88.72 StartY=-9.05 StartZ=0 EndX=88.72 EndY=-21.45 EndZ=0
    g37: LineSegment StartX=91.72 StartY=-24.45 StartZ=0 EndX=104.12 EndY=-24.45 EndZ=0
    g38: LineSegment StartX=107.12 StartY=-21.45 StartZ=0 EndX=107.12 EndY=-9.05 EndZ=0
    g39: LineSegment StartX=104.12 StartY=-6.05 StartZ=0 EndX=91.72 EndY=-6.05 EndZ=0
    g40: ArcOfCircle CenterX=91.72 CenterY=-9.05 CenterZ=0 NormalX=0 NormalY=0 NormalZ=1 AngleXU=0 Radius=3 StartAngle=1.5708 EndAngle=3.14159
    g41: ArcOfCircle CenterX=91.72 CenterY=-21.45 CenterZ=0 NormalX=0 NormalY=0 NormalZ=1 AngleXU=0 Radius=3 StartAngle=3.14159 EndAngle=4.71239
    g42: ArcOfCircle CenterX=104.12 CenterY=-21.45 CenterZ=0 NormalX=0 NormalY=0 NormalZ=1 AngleXU=0 Radius=3 StartAngle=4.71239 EndAngle=6.28319
    g43: ArcOfCircle CenterX=104.12 CenterY=-9.05 CenterZ=0 NormalX=0 NormalY=0 NormalZ=1 AngleXU=0 Radius=3 StartAngle=0 EndAngle=1.5708
    g44: GeomPoint [constr] X=88.72 Y=-6.05 Z=0
    g45: GeomPoint [constr] X=107.12 Y=-24.45 Z=0
    g46: LineSegment StartX=88.52 StartY=-45.08 StartZ=0 EndX=88.52 EndY=-57.48 EndZ=0
    g47: LineSegment StartX=91.52 StartY=-60.48 StartZ=0 EndX=103.92 EndY=-60.48 EndZ=0
    g48: LineSegment StartX=106.92 StartY=-57.48 StartZ=0 EndX=106.92 EndY=-45.08 EndZ=0
    g49: LineSegment StartX=103.92 StartY=-42.08 StartZ=0 EndX=91.52 EndY=-42.08 EndZ=0
    g50: ArcOfCircle CenterX=91.52 CenterY=-45.08 CenterZ=0 NormalX=0 NormalY=0 NormalZ=1 AngleXU=0 Radius=3 StartAngle=1.5708 EndAngle=3.14159
    g51: ArcOfCircle CenterX=91.52 CenterY=-57.48 CenterZ=0 NormalX=0 NormalY=0 NormalZ=1 AngleXU=0 Radius=3 StartAngle=3.14159 EndAngle=4.71239
    g52: ArcOfCircle CenterX=103.92 CenterY=-57.48 CenterZ=0 NormalX=0 NormalY=0 NormalZ=1 AngleXU=0 Radius=3 StartAngle=4.71239 EndAngle=6.28319
    g53: ArcOfCircle CenterX=103.92 CenterY=-45.08 CenterZ=0 NormalX=0 NormalY=0 NormalZ=1 AngleXU=0 Radius=3 StartAngle=0 EndAngle=1.5708
    g54: GeomPoint [constr] X=88.52 Y=-42.08 Z=0
    g55: GeomPoint [constr] X=106.92 Y=-60.48 Z=0
    g56: LineSegment StartX=60.68 StartY=-45.08 StartZ=0 EndX=60.68 EndY=-57.48 EndZ=0
    g57: LineSegment StartX=63.68 StartY=-60.48 StartZ=0 EndX=76.08 EndY=-60.48 EndZ=0
    g58: LineSegment StartX=79.08 StartY=-57.48 StartZ=0 EndX=79.08 EndY=-45.08 EndZ=0
    g59: LineSegment StartX=76.08 StartY=-42.08 StartZ=0 EndX=63.68 EndY=-42.08 EndZ=0
    g60: ArcOfCircle CenterX=63.68 CenterY=-45.08 CenterZ=0 NormalX=0 NormalY=0 NormalZ=1 AngleXU=0 Radius=3 StartAngle=1.5708 EndAngle=3.14159
    g61: ArcOfCircle CenterX=63.68 CenterY=-57.48 CenterZ=0 NormalX=0 NormalY=0 NormalZ=1 AngleXU=0 Radius=3 StartAngle=3.14159 EndAngle=4.71239
    g62: ArcOfCircle CenterX=76.08 CenterY=-57.48 CenterZ=0 NormalX=0 NormalY=0 NormalZ=1 AngleXU=0 Radius=3 StartAngle=4.71239 EndAngle=6.28319
    g63: ArcOfCircle CenterX=76.08 CenterY=-45.08 CenterZ=0 NormalX=0 NormalY=0 NormalZ=1 AngleXU=0 Radius=3 StartAngle=0 EndAngle=1.5708
    g64: GeomPoint [constr] X=60.68 Y=-42.08 Z=0
    g65: GeomPoint [constr] X=79.08 Y=-60.48 Z=0
    g66: LineSegment StartX=32.84 StartY=-45.08 StartZ=0 EndX=32.84 EndY=-57.48 EndZ=0
    g67: LineSegment StartX=35.84 StartY=-60.48 StartZ=0 EndX=48.24 EndY=-60.48 EndZ=0
    g68: LineSegment StartX=51.24 StartY=-57.48 StartZ=0 EndX=51.24 EndY=-45.08 EndZ=0
    g69: LineSegment StartX=48.24 StartY=-42.08 StartZ=0 EndX=35.84 EndY=-42.08 EndZ=0
    g70: ArcOfCircle CenterX=35.84 CenterY=-45.08 CenterZ=0 NormalX=0 NormalY=0 NormalZ=1 AngleXU=0 Radius=3 StartAngle=1.5708 EndAngle=3.14159
    g71: ArcOfCircle CenterX=35.84 CenterY=-57.48 CenterZ=0 NormalX=0 NormalY=0 NormalZ=1 AngleXU=0 Radius=3 StartAngle=3.14159 EndAngle=4.71239
    g72: ArcOfCircle CenterX=48.24 CenterY=-57.48 CenterZ=0 NormalX=0 NormalY=0 NormalZ=1 AngleXU=0 Radius=3 StartAngle=4.71239 EndAngle=6.28319
    g73: ArcOfCircle CenterX=48.24 CenterY=-45.08 CenterZ=0 NormalX=0 NormalY=0 NormalZ=1 AngleXU=0 Radius=3 StartAngle=0 EndAngle=1.5708
    g74: GeomPoint [constr] X=32.84 Y=-42.08 Z=0
    g75: GeomPoint [constr] X=51.24 Y=-60.48 Z=0
    g76: LineSegment StartX=5 StartY=-45.08 StartZ=0 EndX=5 EndY=-57.48 EndZ=0
    g77: LineSegment StartX=8 StartY=-60.48 StartZ=0 EndX=20.4 EndY=-60.48 EndZ=0
    g78: LineSegment StartX=23.4 StartY=-57.48 StartZ=0 EndX=23.4 EndY=-45.08 EndZ=0
    g79: LineSegment StartX=20.4 StartY=-42.08 StartZ=0 EndX=8 EndY=-42.08 EndZ=0
    g80: ArcOfCircle CenterX=8 CenterY=-45.08 CenterZ=0 NormalX=0 NormalY=0 NormalZ=1 AngleXU=0 Radius=3 StartAngle=1.5708 EndAngle=3.14159
    g81: ArcOfCircle CenterX=8 CenterY=-57.48 CenterZ=0 NormalX=0 NormalY=0 NormalZ=1 AngleXU=0 Radius=3 StartAngle=3.14159 EndAngle=4.71239
    g82: ArcOfCircle CenterX=20.4 CenterY=-57.48 CenterZ=0 NormalX=0 NormalY=0 NormalZ=1 AngleXU=0 Radius=3 StartAngle=4.71239 EndAngle=6.28319
    g83: ArcOfCircle CenterX=20.4 CenterY=-45.08 CenterZ=0 NormalX=0 NormalY=0 NormalZ=1 AngleXU=0 Radius=3 StartAngle=7e-16 EndAngle=1.5708
    g84: GeomPoint [constr] X=5 Y=-42.08 Z=0
    g85: GeomPoint [constr] X=23.4 Y=-60.48 Z=0
    g86: GeomPoint X=42.24 Y=-15.25 Z=0
    g87: GeomPoint X=70.08 Y=-15.25 Z=0
    g88: GeomPoint X=97.92 Y=-15.25 Z=0
    g89: GeomPoint X=14.2 Y=-51.28 Z=0
    g90: GeomPoint X=42.04 Y=-51.28 Z=0
    g91: GeomPoint X=69.88 Y=-51.28 Z=0
    g92: GeomPoint X=97.72 Y=-51.28 Z=0
  constraints (203):
    c: Coincident(g0,g1)
    c: Coincident(g1,g2)
    c: Coincident(g2,g3)
    c: Coincident(g3,g0)
    c: Vertical(g0)
    c: Vertical(g2)
    c: Horizontal(g1)
    c: Horizontal(g3)
    c: Coincident(g0,g-11)
    c: Coincident(g1,g-12)
    c: Tangent(g4,g8) = -1.5708
    c: Tangent(g4,g9) = -1.5708
    c: Tangent(g5,g9) = -1.5708
    c: Tangent(g5,g10) = -1.5708
    c: Tangent(g6,g10) = -1.5708
    c: Tangent(g6,g11) = -1.5708
    c: Tangent(g7,g11) = -1.5708
    c: Tangent(g7,g8) = -1.5708
    c: Vertical(g4)
    c: Vertical(g6)
    c: Horizontal(g5)
    c: Horizontal(g7)
    c: Equal(g8,g9)
    c: Equal(g9,g10)
    c: Equal(g10,g11)
    c: PointOnObject(g12,g4)
    c: PointOnObject(g12,g7)
    c: PointOnObject(g13,g5)
    c: PointOnObject(g13,g6)
    c: Radius(g11) = 3
    c: DistanceY(g5,g7) = 18.4
    c: DistanceX(g4,g6) = 18.4
    c: Symmetric(g8,g10,g14)
    c: Symmetric(g-4,g-8,g15)
    c: Coincident(g14,g15)
    c: Tangent(g16,g20) = -1.5708
    c: Tangent(g16,g21) = -1.5708
    c: Tangent(g17,g21) = -1.5708
    c: Tangent(g17,g22) = -1.5708
    c: Tangent(g18,g22) = -1.5708
    c: Tangent(g18,g23) = -1.5708
    c: Tangent(g19,g23) = -1.5708
    c: Tangent(g19,g20) = -1.5708
    c: Vertical(g16)
    c: Vertical(g18)
    c: Horizontal(g17)
    c: Horizontal(g19)
    c: Equal(g20,g21)
    c: Equal(g21,g22)
    c: Equal(g22,g23)
    c: PointOnObject(g24,g16)
    c: PointOnObject(g24,g19)
    c: PointOnObject(g25,g17)
    c: PointOnObject(g25,g18)
    c: Tangent(g26,g30) = -1.5708
    c: Tangent(g26,g31) = -1.5708
    c: Tangent(g27,g31) = -1.5708
    c: Tangent(g27,g32) = -1.5708
    c: Tangent(g28,g32) = -1.5708
    c: Tangent(g28,g33) = -1.5708
    c: Tangent(g29,g33) = -1.5708
    c: Tangent(g29,g30) = -1.5708
    c: Vertical(g26)
    c: Vertical(g28)
    c: Horizontal(g27)
    c: Horizontal(g29)
    c: Equal(g30,g31)
    c: Equal(g31,g32)
    c: Equal(g32,g33)
    c: PointOnObject(g34,g26)
    c: PointOnObject(g34,g29)
    c: PointOnObject(g35,g27)
    c: PointOnObject(g35,g28)
    c: Tangent(g36,g40) = -1.5708
    c: Tangent(g36,g41) = -1.5708
    c: Tangent(g37,g41) = -1.5708
    c: Tangent(g37,g42) = -1.5708
    c: Tangent(g38,g42) = -1.5708
    c: Tangent(g38,g43) = -1.5708
    c: Tangent(g39,g43) = -1.5708
    c: Tangent(g39,g40) = -1.5708
    c: Vertical(g36)
    c: Vertical(g38)
    c: Horizontal(g37)
    c: Horizontal(g39)
    c: Equal(g40,g41)
    c: Equal(g41,g42)
    c: Equal(g42,g43)
    c: PointOnObject(g44,g36)
    c: PointOnObject(g44,g39)
    c: PointOnObject(g45,g37)
    c: PointOnObject(g45,g38)
    c: Tangent(g46,g50) = -1.5708
    c: Tangent(g46,g51) = -1.5708
    c: Tangent(g47,g51) = -1.5708
    c: Tangent(g47,g52) = -1.5708
    c: Tangent(g48,g52) = -1.5708
    c: Tangent(g48,g53) = -1.5708
    c: Tangent(g49,g53) = -1.5708
    c: Tangent(g49,g50) = -1.5708
    c: Vertical(g46)
    c: Vertical(g48)
    c: Horizontal(g47)
    c: Horizontal(g49)
    c: Equal(g50,g51)
    c: Equal(g51,g52)
    c: Equal(g52,g53)
    c: PointOnObject(g54,g46)
    c: PointOnObject(g54,g49)
    c: PointOnObject(g55,g47)
    c: PointOnObject(g55,g48)
    c: Tangent(g56,g60) = -1.5708
    c: Tangent(g56,g61) = -1.5708
    c: Tangent(g57,g61) = -1.5708
    c: Tangent(g57,g62) = -1.5708
    c: Tangent(g58,g62) = -1.5708
    c: Tangent(g58,g63) = -1.5708
    c: Tangent(g59,g63) = -1.5708
    c: Tangent(g59,g60) = -1.5708
    c: Vertical(g56)
    c: Vertical(g58)
    c: Horizontal(g57)
    c: Horizontal(g59)
    c: Equal(g60,g61)
    c: Equal(g61,g62)
    c: Equal(g62,g63)
    c: PointOnObject(g64,g56)
    c: PointOnObject(g64,g59)
    c: PointOnObject(g65,g57)
    c: PointOnObject(g65,g58)
    c: Tangent(g66,g70) = -1.5708
    c: Tangent(g66,g71) = -1.5708
    c: Tangent(g67,g71) = -1.5708
    c: Tangent(g67,g72) = -1.5708
    c: Tangent(g68,g72) = -1.5708
    c: Tangent(g68,g73) = -1.5708
    c: Tangent(g69,g73) = -1.5708
    c: Tangent(g69,g70) = -1.5708
    c: Vertical(g66)
    c: Vertical(g68)
    c: Horizontal(g67)
    c: Horizontal(g69)
    c: Equal(g70,g71)
    c: Equal(g71,g72)
    c: Equal(g72,g73)
    c: PointOnObject(g74,g66)
    c: PointOnObject(g74,g69)
    c: PointOnObject(g75,g67)
    c: PointOnObject(g75,g68)
    c: Tangent(g76,g80) = -1.5708
    c: Tangent(g76,g81) = -1.5708
    c: Tangent(g77,g81) = -1.5708
    c: Tangent(g77,g82) = -1.5708
    c: Tangent(g78,g82) = -1.5708
    c: Tangent(g78,g83) = -1.5708
    c: Tangent(g79,g83) = -1.5708
    c: Tangent(g79,g80) = -1.5708
    c: Vertical(g76)
    c: Vertical(g78)
    c: Horizontal(g77)
    c: Horizontal(g79)
    c: Equal(g80,g81)
    c: Equal(g81,g82)
    c: Equal(g82,g83)
    c: PointOnObject(g84,g76)
    c: PointOnObject(g84,g79)
    c: PointOnObject(g85,g77)
    c: PointOnObject(g85,g78)
    c: Equal(g11,g23)
    c: Equal(g23,g33)
    c: Equal(g33,g43)
    c: Equal(g43,g53)
    c: Equal(g53,g63)
    c: Equal(g63,g73)
    c: Equal(g73,g83)
    c: Equal(g7,g19)
    c: Equal(g19,g29)
    c: Equal(g29,g39)
    c: Equal(g39,g49)
    c: Equal(g49,g59)
    c: Equal(g59,g79)
    c: Equal(g76,g66)
    c: Equal(g66,g56)
    c: Equal(g56,g46)
    c: Equal(g46,g36)
    c: Equal(g36,g26)
    c: Equal(g26,g16)
    c: Equal(g16,g4)
    c: Equal(g59,g69)
    c: Symmetric(g-14,g-18,g86)
    c: Symmetric(g20,g22,g86)
    c: Symmetric(g-22,g-26,g87)
    c: Symmetric(g30,g32,g87)
    c: Symmetric(g-29,g-33,g88)
    c: Symmetric(g40,g42,g88)
    c: Symmetric(g-61,g-65,g89)
    c: Symmetric(g-60,g-56,g90)
    c: Symmetric(g-47,g-51,g91)
    c: Symmetric(g-44,g-40,g92)
    c: Symmetric(g50,g52,g92)
    c: Symmetric(g60,g62,g91)
    c: Symmetric(g70,g72,g90)
    c: Symmetric(g80,g82,g89)
FEATURE [PartDesign::Pad] Pad025  label="PadButtonSlideChannel"
  BaseFeature = -> Pad024
  Direction = (0,0,1)
  Length = 1.59
  Length2 = 10
  Profile = -> Sketch034
  ReferenceAxis = -> Sketch034 [N_Axis]
  Refine = true
  SideType = 0
  Suppressed = false
  Type = 0
  Type2 = 0
  expr: Length = <<VarSetButtonDimensions>>.Base_button_slide_depth + <<VarSetButtonDimensions>>.Base_base_thickness
FEATURE [PartDesign::Plane] DatumPlane003  label="DatumPlaneForMirroring"
  AttachmentSupport = -> [Pad025]
  Length = 165.309
  MapMode = 5
  Placement = pos=(0,0,3.09) rot=(0,0,1;0rad)
  ResizeMode = 0
  Width = 120.249
FEATURE [PartDesign::Mirrored] Mirrored004
  BaseFeature = -> Pad025
  MirrorPlane = -> DatumPlane003
  Originals = -> [Pad024,Pad025]
  Refine = true
  Suppressed = false
  TransformMode = 0
FEATURE [PartDesign::SubShapeBinder] Binder007  label="BinderPcbV2"
  BindCopyOnChange = 0
  BindMode = 0
  ClaimChildren = false
  Context = -> Body003 [Binder007.]
  Fuse = false
  MakeFace = true
  OffsetFill = false
  OffsetIntersection = false
  OffsetJoinType = 0
  OffsetOpenResult = false
  PartialLoad = false
  Placement = pos=(0.66,0,0) rot=(0,0,1;0rad)
  Refine = true
  Relative = true
  Support = -> [Board_cc028]
  _Version = 2
FEATURE [Sketcher::SketchObject] Sketch040  label="SketchPcbStandOffs001"
  ArcFitTolerance = 1e-06
  AttachmentSupport = -> [Mirrored004]
  ExternalGeometry = -> [Mirrored004,Binder007]
  ExternalTypes = [0]
  FullyConstrained = true
  MakeInternals = false
  MapMode = 5
  Placement = pos=(0,0,0) rot=(1,0,0;3.14159rad)
  sketch-geometry (8):
    g0: Circle CenterX=5.17408 CenterY=61.5799 CenterZ=0 NormalX=0 NormalY=0 NormalZ=1 AngleXU=0 Radius=1
    g1: Circle CenterX=5.17408 CenterY=5.02733 CenterZ=0 NormalX=0 NormalY=0 NormalZ=1 AngleXU=0 Radius=1
    g2: Circle CenterX=108.174 CenterY=5.02733 CenterZ=0 NormalX=0 NormalY=0 NormalZ=1 AngleXU=0 Radius=1
    g3: Circle CenterX=108.174 CenterY=61.5799 CenterZ=0 NormalX=0 NormalY=0 NormalZ=1 AngleXU=0 Radius=1
    g4: Circle CenterX=5.17408 CenterY=61.5799 CenterZ=0 NormalX=0 NormalY=0 NormalZ=1 AngleXU=0 Radius=2.5
    g5: Circle CenterX=5.17408 CenterY=5.02733 CenterZ=0 NormalX=0 NormalY=0 NormalZ=1 AngleXU=0 Radius=2.5
    g6: Circle CenterX=108.174 CenterY=5.02733 CenterZ=0 NormalX=0 NormalY=0 NormalZ=1 AngleXU=0 Radius=2.5
    g7: Circle CenterX=108.174 CenterY=61.5799 CenterZ=0 NormalX=0 NormalY=0 NormalZ=1 AngleXU=0 Radius=2.5
  constraints (17):
    c: Diameter(g0) = 2
    c: Equal(g0,g1)
    c: Equal(g1,g2)
    c: Equal(g2,g3)
    c: Coincident(g4,g0)
    c: Diameter(g4) = 5
    c: Coincident(g5,g1)
    c: Coincident(g6,g2)
    c: Coincident(g7,g3)
    c: Equal(g4,g7)
    c: Equal(g7,g6)
    c: Equal(g6,g5)
    c: Coincident(g3,g-5)
    c: Coincident(g-6,g2)
    c: Coincident(g1,g-7)
    c: Coincident(g0,g-8)
    c: DistanceX(g1,g2) = 103
FEATURE [PartDesign::Pad] Pad029  label="PadStandoffs"
  BaseFeature = -> Mirrored004
  Direction = (0,0,-1)
  Length = 3.2
  Length2 = 10
  Profile = -> Sketch040
  ReferenceAxis = -> Sketch040 [N_Axis]
  Refine = true
  SideType = 0
  Suppressed = false
  Type = 0
  Type2 = 0
FEATURE [PartDesign::Pocket] Pocket007  label="PocketHeatInsertHole"
  BaseFeature = -> Pad029
  Direction = (0,0,1)
  Length = 6.5
  Length2 = 5
  Profile = -> Pad029 [Face230,Face228,Face227,Face229]
  Refine = true
  SideType = 0
  Suppressed = false
  Type = 0
  Type2 = 0
FEATURE [Sketcher::SketchObject] Sketch041  label="SketchSidewalls"
  ArcFitTolerance = 1e-06
  AttachmentSupport = -> [Pocket007]
  ExternalGeometry = -> [Pocket007]
  ExternalTypes = [0]
  FullyConstrained = true
  MakeInternals = false
  MapMode = 5
  Placement = pos=(0,0,0) rot=(1,0,0;3.14159rad)
  sketch-geometry (8):
    g0: LineSegment StartX=-3 StartY=71.81 StartZ=0 EndX=-3 EndY=-6 EndZ=0
    g1: LineSegment StartX=-3 StartY=-6 StartZ=0 EndX=116.87 EndY=-6 EndZ=0
    g2: LineSegment StartX=116.87 StartY=-6 StartZ=0 EndX=116.87 EndY=71.81 EndZ=0
    g3: LineSegment StartX=116.87 StartY=71.81 StartZ=0 EndX=-3 EndY=71.81 EndZ=0
    g4: LineSegment StartX=-1 StartY=69.81 StartZ=0 EndX=-1 EndY=-4 EndZ=0
    g5: LineSegment StartX=-1 StartY=-4 StartZ=0 EndX=114.87 EndY=-4 EndZ=0
    g6: LineSegment StartX=114.87 StartY=-4 StartZ=0 EndX=114.87 EndY=69.81 EndZ=0
    g7: LineSegment StartX=114.87 StartY=69.81 StartZ=0 EndX=-1 EndY=69.81 EndZ=0
  constraints (22):
    c: Coincident(g0,g1)
    c: Coincident(g1,g2)
    c: Coincident(g2,g3)
    c: Coincident(g3,g0)
    c: Vertical(g0)
    c: Vertical(g2)
    c: Horizontal(g1)
    c: Horizontal(g3)
    c: Coincident(g0,g-3)
    c: Coincident(g1,g-4)
    c: Coincident(g4,g5)
    c: Coincident(g5,g6)
    c: Coincident(g6,g7)
    c: Coincident(g7,g4)
    c: Vertical(g4)
    c: Vertical(g6)
    c: Horizontal(g5)
    c: Horizontal(g7)
    c: DistanceX(g5,g1) = 2
    c: DistanceY(g1,g5) = 2
    c: DistanceY(g4,g0) = 2
    c: DistanceX(g0,g4) = 2
FEATURE [PartDesign::Pad] Pad030  label="PadSidewalls"
  BaseFeature = -> Pocket007
  Direction = (0,0,-1)
  Length = 8
  Length2 = 10
  Profile = -> Sketch041
  ReferenceAxis = -> Sketch041 [N_Axis]
  Refine = true
  SideType = 0
  Suppressed = false
  Type = 0
  Type2 = 0
FEATURE [Sketcher::SketchObject] Sketch042  label="SketchCaseBackCoverHoles"
  ArcFitTolerance = 1e-06
  AttachmentSupport = -> [Pad030]
  ExternalGeometry = -> [Binder006,Pad030]
  ExternalTypes = [0]
  FullyConstrained = true
  MakeInternals = false
  MapMode = 5
  Placement = pos=(0,0,0) rot=(1,0,0;3.14159rad)
  sketch-geometry (14):
    g0: GeomPoint X=57.16 Y=32.925 Z=0
    g1: GeomPoint [constr] X=57.16 Y=32.925 Z=0
    g2: Circle CenterX=113.57 CenterY=68.81 CenterZ=0 NormalX=0 NormalY=0 NormalZ=1 AngleXU=0 Radius=1
    g3: Circle CenterX=2e-16 CenterY=68.81 CenterZ=0 NormalX=0 NormalY=0 NormalZ=1 AngleXU=0 Radius=1
    g4: Circle CenterX=2e-16 CenterY=-2.7 CenterZ=0 NormalX=0 NormalY=0 NormalZ=1 AngleXU=0 Radius=1
    g5: Circle CenterX=113.57 CenterY=-2.7 CenterZ=0 NormalX=0 NormalY=0 NormalZ=1 AngleXU=0 Radius=1
    g6: Circle CenterX=113.57 CenterY=68.81 CenterZ=0 NormalX=0 NormalY=0 NormalZ=1 AngleXU=0 Radius=2.5
    g7: Circle CenterX=113.57 CenterY=-2.7 CenterZ=0 NormalX=0 NormalY=0 NormalZ=1 AngleXU=0 Radius=2.5
    g8: Circle CenterX=2e-16 CenterY=-2.7 CenterZ=0 NormalX=0 NormalY=0 NormalZ=1 AngleXU=0 Radius=2.5
    g9: Circle CenterX=2e-16 CenterY=68.81 CenterZ=0 NormalX=0 NormalY=0 NormalZ=1 AngleXU=0 Radius=2.5
    g10: LineSegment [constr] StartX=2e-16 StartY=68.81 StartZ=0 EndX=2e-16 EndY=-2.7 EndZ=0
    g11: LineSegment [constr] StartX=2e-16 StartY=-2.7 StartZ=0 EndX=113.57 EndY=-2.7 EndZ=0
    g12: LineSegment [constr] StartX=113.57 StartY=-2.7 StartZ=0 EndX=113.57 EndY=68.81 EndZ=0
    g13: LineSegment [constr] StartX=113.57 StartY=68.81 StartZ=0 EndX=0 EndY=68.81 EndZ=0
  constraints (30):
    c: Symmetric(g-3,g-4,g0)
    c: Coincident(g1,g0)
    c: Diameter(g2) = 2
    c: Equal(g2,g5)
    c: Equal(g5,g4)
    c: Equal(g4,g3)
    c: Diameter(g6) = 5
    c: Equal(g6,g9)
    c: Equal(g9,g8)
    c: Equal(g8,g7)
    c: Coincident(g3,g9)
    c: Coincident(g6,g2)
    c: Coincident(g7,g5)
    c: Coincident(g8,g4)
    c: Coincident(g10,g11)
    c: Coincident(g11,g12)
    c: Coincident(g12,g13)
    c: Coincident(g13,g10)
    c: Vertical(g10)
    c: Vertical(g12)
    c: Horizontal(g11)
    c: Horizontal(g13)
    c: DistanceX(g11,g-7) = 3.3
    c: DistanceY(g-7,g11) = 3.3
    c: DistanceX(g-5,g10) = 3
    c: DistanceY(g10,g-5) = 3
    c: Coincident(g11,g5)
    c: Coincident(g3,g10)
    c: Coincident(g2,g12)
    c: Coincident(g4,g10)
FEATURE [PartDesign::Pad] Pad031  label="PadCaseBackingMountHoles"
  BaseFeature = -> Pad030
  Direction = (0,0,-1)
  Length = 8
  Length2 = 10
  Profile = -> Sketch042
  ReferenceAxis = -> Sketch042 [N_Axis]
  Refine = true
  SideType = 0
  Suppressed = false
  Type = 0
  Type2 = 0
FEATURE [Sketcher::SketchObject] Sketch043
  ArcFitTolerance = 1e-06
  AttachmentSupport = -> [Pad031]
  ExternalGeometry = -> [Pad031]
  ExternalTypes = [0]
  FullyConstrained = true
  MakeInternals = false
  MapMode = 5
  Placement = pos=(0,4,0) rot=(1,0,0;1.5708rad)
  sketch-geometry (12):
    g0: GeomPoint X=56.785 Y=-8 Z=0
    g1: LineSegment StartX=49.285 StartY=-1.3 StartZ=0 EndX=49.285 EndY=-6.5 EndZ=0
    g2: LineSegment StartX=49.285 StartY=-6.5 StartZ=0 EndX=64.285 EndY=-6.5 EndZ=0
    g3: LineSegment StartX=64.285 StartY=-6.5 StartZ=0 EndX=64.285 EndY=-1.3 EndZ=0
    g4: LineSegment StartX=64.285 StartY=-1.3 StartZ=0 EndX=58.085 EndY=-1.3 EndZ=0
    g5: LineSegment StartX=58.085 StartY=-1.3 StartZ=0 EndX=58.085 EndY=-0.3 EndZ=0
    g6: LineSegment StartX=58.085 StartY=-0.3 StartZ=0 EndX=55.485 EndY=-0.3 EndZ=0
    g7: LineSegment StartX=55.485 StartY=-0.3 StartZ=0 EndX=55.485 EndY=-1.3 EndZ=0
    g8: LineSegment StartX=55.485 StartY=-1.3 StartZ=0 EndX=49.285 EndY=-1.3 EndZ=0
    g9: GeomPoint X=56.785 Y=-3.9 Z=0
    g10: GeomPoint X=56.785 Y=-0.3 Z=0
    g11: GeomPoint X=56.785 Y=-8 Z=0
  constraints (28):
    c: Coincident(g1,g2)
    c: Coincident(g2,g3)
    c: Coincident(g3,g4)
    c: Coincident(g8,g1)
    c: Vertical(g1)
    c: Vertical(g3)
    c: Horizontal(g2)
    c: Horizontal(g4)
    c: Coincident(g5,g6)
    c: Coincident(g6,g7)
    c: Horizontal(g6)
    c: Vertical(g5)
    c: Vertical(g7)
    c: Coincident(g8,g7)
    c: Horizontal(g8)
    c: Horizontal(g7,g4)
    c: Symmetric(g1,g2,g9)
    c: Symmetric(g6,g5,g10)
    c: Coincident(g5,g4)
    c: DistanceY(g5,g5) = 1
    c: DistanceX(g6,g6) = 2.6
    c: DistanceY(g3,g3) = 5.2
    c: DistanceX(g2,g2) = 15
    c: Vertical(g10,g9)
    c: Vertical(g9,g0)
    c: DistanceY(g0,g2) = 1.5
    c: Symmetric(g-3,g-3,g11)
    c: Coincident(g0,g11)
FEATURE [PartDesign::Pocket] Pocket008  label="PocketWiringOpening"
  BaseFeature = -> Pad031
  Direction = (0,1,-2e-16)
  Length = 5
  Length2 = 5
  Profile = -> Sketch043
  ReferenceAxis = -> Sketch043 [N_Axis]
  Refine = true
  SideType = 0
  Suppressed = false
  Type = 2
  Type2 = 0
FEATURE [Sketcher::SketchObject] Sketch048
  ArcFitTolerance = 1e-06
  ExternalTypes = [0]
  FullyConstrained = true
  MakeInternals = false
  MapMode = 5
  Placement = pos=(0,0,6.18) rot=(0,0,1;0rad)
  sketch-geometry (4):
    g0: Circle CenterX=5.17408 CenterY=-5.02733 CenterZ=0 NormalX=0 NormalY=0 NormalZ=1 AngleXU=0 Radius=1.6
    g1: Circle CenterX=5.17408 CenterY=-61.5799 CenterZ=0 NormalX=0 NormalY=0 NormalZ=1 AngleXU=0 Radius=1.6
    g2: Circle CenterX=108.174 CenterY=-61.5799 CenterZ=0 NormalX=0 NormalY=0 NormalZ=1 AngleXU=0 Radius=1.6
    g3: Circle CenterX=108.174 CenterY=-5.02733 CenterZ=0 NormalX=0 NormalY=0 NormalZ=1 AngleXU=0 Radius=1.6
  constraints (8):
    c: Coincident(g0,g-3)
    c: Equal(g0,g-3)
    c: Coincident(g1,g-4)
    c: Equal(g1,g-4)
    c: Coincident(g2,g-5)
    c: Equal(g2,g-5)
    c: Coincident(g3,g-6)
    c: Equal(g3,g-6)
FEATURE [PartDesign::Pad] Pad033  label="PadFaceHoleFill"
  BaseFeature = -> Pocket008
  Direction = (0,0,1)
  Length = 1.5
  Length2 = 10
  Profile = -> Sketch048
  ReferenceAxis = -> Sketch048 [N_Axis]
  Refine = true
  Reversed = true
  SideType = 0
  Suppressed = false
  Type = 0
  Type2 = 0
  expr: Length = <<VarSetButtonDimensions>>.button_cap_wall_thickness
FEATURE [Sketcher::SketchObject] Sketch049  label="SketchPcbStopBar"
  ArcFitTolerance = 1e-06
  AttachmentSupport = -> [Pad033]
  ExternalGeometry = -> [Pad033]
  ExternalTypes = [0]
  FullyConstrained = true
  MakeInternals = false
  MapMode = 5
  Placement = pos=(0,0,0) rot=(1,0,0;3.14159rad)
  expr: Constraints[11] = <<VarSetButtonDimensions>>.button_cap_wall_thickness
  sketch-geometry (6):
    g0: LineSegment StartX=11.935 StartY=64.56 StartZ=0 EndX=11.935 EndY=66.06 EndZ=0
    g1: LineSegment StartX=11.935 StartY=66.06 StartZ=0 EndX=101.935 EndY=66.06 EndZ=0
    g2: LineSegment StartX=101.935 StartY=66.06 StartZ=0 EndX=101.935 EndY=64.56 EndZ=0
    g3: LineSegment StartX=101.935 StartY=64.56 StartZ=0 EndX=11.935 EndY=64.56 EndZ=0
    g4: GeomPoint [constr] X=56.935 Y=65.31 Z=0
    g5: GeomPoint X=56.935 Y=71.81 Z=0
  constraints (14):
    c: Coincident(g0,g1)
    c: Coincident(g1,g2)
    c: Coincident(g2,g3)
    c: Coincident(g3,g0)
    c: Vertical(g0)
    c: Vertical(g2)
    c: Horizontal(g1)
    c: Horizontal(g3)
    c: Symmetric(g2,g0,g4)
    c: Symmetric(g-3,g-3,g5)
    c: Vertical(g4,g5)
    c: DistanceY(g2,g2) = 1.5
    c: DistanceX(g3,g3) = 90
    c: Distance(g4,g5) = 6.5
FEATURE [PartDesign::Pad] Pad034  label="PadPcbStopBar"
  BaseFeature = -> Pad033
  Direction = (0,0,-1)
  Length = 3.2
  Length2 = 10
  Profile = -> Sketch049
  ReferenceAxis = -> Sketch049 [N_Axis]
  Refine = true
  SideType = 0
  Suppressed = false
  Type = 0
  Type2 = 0
FEATURE [PartDesign::Plane] DatumPlane
  AttachmentOffset = pos=(0,0,-38.905) rot=(0,0,1;0rad)
  AttachmentSupport = -> [Pad034]
  Length = 158.715
  MapMode = 5
  Placement = pos=(0,-32.905,-8.6e-15) rot=(1,0,0;1.5708rad)
  ResizeMode = 0
  Width = 66.8446
FEATURE [PartDesign::Mirrored] Mirrored
  BaseFeature = -> Pad034
  MirrorPlane = -> DatumPlane
  Originals = -> [Pad034]
  Refine = true
  Suppressed = false
  TransformMode = 0
FEATURE [Sketcher::SketchObject] Sketch053  label="SketchProgrammingOpening"
  ArcFitTolerance = 1e-06
  AttachmentSupport = -> [Mirrored]
  ExternalGeometry = -> [Binder006,Mirrored]
  ExternalTypes = [0]
  FullyConstrained = true
  MakeInternals = false
  MapMode = 5
  Placement = pos=(116.87,0,0) rot=(0.57735,0.57735,0.57735;2.0944rad)
  sketch-geometry (6):
    g0: LineSegment StartX=-40.71 StartY=-4.7 StartZ=0 EndX=-40.71 EndY=-8 EndZ=0
    g1: LineSegment StartX=-40.71 StartY=-8 StartZ=0 EndX=-24.71 EndY=-8 EndZ=0
    g2: LineSegment StartX=-24.71 StartY=-8 StartZ=0 EndX=-24.71 EndY=-4.7 EndZ=0
    g3: LineSegment StartX=-24.71 StartY=-4.7 StartZ=0 EndX=-40.71 EndY=-4.7 EndZ=0
    g4: GeomPoint X=-32.71 Y=-6.35 Z=0
    g5: GeomPoint X=-32.71 Y=-4.91 Z=0
  constraints (14):
    c: Coincident(g0,g1)
    c: Coincident(g1,g2)
    c: Coincident(g2,g3)
    c: Coincident(g3,g0)
    c: Vertical(g0)
    c: Vertical(g2)
    c: Horizontal(g1)
    c: Horizontal(g3)
    c: DistanceX(g1,g1) = 16
    c: DistanceY(g2,g2) = 3.3
    c: PointOnObject(g1,g-9)
    c: Symmetric(g0,g1,g4)
    c: Symmetric(g-6,g-8,g5)
    c: Vertical(g4,g5)
FEATURE [PartDesign::Pocket] Pocket014  label="PocketProgrammingOpening"
  BaseFeature = -> Mirrored
  Direction = (-1,0,0)
  Length = 5
  Length2 = 5
  Profile = -> Sketch053
  ReferenceAxis = -> Sketch053 [N_Axis]
  Refine = true
  SideType = 0
  Suppressed = false
  Type = 2
  Type2 = 0
FEATURE [Sketcher::SketchObject] Sketch082  label="SketchConnectorClearance"
  ArcFitTolerance = 1e-06
  AttachmentSupport = -> [Pocket014]
  ExternalGeometry = -> [Pocket014]
  ExternalTypes = [0]
  FullyConstrained = true
  MakeInternals = false
  MapMode = 5
  Placement = pos=(0,-1.25,5e-16) rot=(1,0,0;1.5708rad)
  sketch-geometry (4):
    g0: LineSegment StartX=66.785 StartY=-3.2 StartZ=0 EndX=66.785 EndY=0 EndZ=0
    g1: LineSegment StartX=66.785 StartY=0 StartZ=0 EndX=46.785 EndY=0 EndZ=0
    g2: LineSegment StartX=46.785 StartY=0 StartZ=0 EndX=46.785 EndY=-3.2 EndZ=0
    g3: LineSegment StartX=46.785 StartY=-3.2 StartZ=0 EndX=66.785 EndY=-3.2 EndZ=0
  constraints (12):
    c: Coincident(g0,g1)
    c: Coincident(g1,g2)
    c: Coincident(g2,g3)
    c: Coincident(g3,g0)
    c: Vertical(g0)
    c: Vertical(g2)
    c: Horizontal(g1)
    c: Horizontal(g3)
    c: PointOnObject(g0,g-1)
    c: PointOnObject(g0,g-5)
    c: DistanceX(g2,g-4) = 2.5
    c: DistanceX(g-3,g0) = 2.5
FEATURE [PartDesign::Pocket] Pocket034  label="PocketConnectorClearance"
  BaseFeature = -> Pocket014
  Direction = (0,1,-2e-16)
  Length = 5
  Length2 = 5
  Profile = -> Sketch082
  ReferenceAxis = -> Sketch082 [N_Axis]
  Refine = true
  SideType = 0
  Suppressed = false
  Type = 2
  Type2 = 0
FEATURE [PartDesign::Fillet] Fillet
  Base = -> Pocket034 [Edge91,Edge94,Edge101,Edge92]
  BaseFeature = -> Pocket034
  Radius = 3
  Refine = true
  SupportTransform = false
  Suppressed = false
  UseAllEdges = false
FEATURE [PartDesign::Chamfer] Chamfer
  Angle = 45
  Base = -> Fillet [Edge1,Edge2,Edge4,Edge6,Edge8,Edge3,Edge5,Edge7]
  BaseFeature = -> Fillet
  ChamferType = 0
  FlipDirection = false
  Refine = true
  Size = 3
  Size2 = 1
  SupportTransform = false
  Suppressed = false
  UseAllEdges = false
FEATURE [Part::Part2DObjectPython] ShapeString  label="ShapeStringUnderCabinet"  # Draft 2D object (typed FeaturePython)
  FontFile = /Library/Fonts/Arial Unicode.ttf
  Fuse = false
  Justification = 6
  JustificationReference = 0
  KeepLeftMargin = false
  MakeFace = true
  ObliqueAngle = 0
  Placement = pos=(6.21,-31.23,6.18) rot=(0,0,1;0rad)
  ScaleToSize = true
  Size = 3
  String = Cabinet
  Tracking = 0
FEATURE [Part::Part2DObjectPython] ShapeString001  label="ShapeStringKitchen"  # Draft 2D object (typed FeaturePython)
  FontFile = /Library/Fonts/Arial Unicode.ttf
  Fuse = false
  Justification = 6
  JustificationReference = 0
  KeepLeftMargin = false
  MakeFace = true
  ObliqueAngle = 0
  Placement = pos=(35.75,-30.81,6.18) rot=(0,0,1;0rad)
  ScaleToSize = true
  Size = 3
  String = Kitchen
  Tracking = 0
FEATURE [Part::Part2DObjectPython] ShapeString002  label="ShapeStringEntry"  # Draft 2D object (typed FeaturePython)
  FontFile = /Library/Fonts/Arial Unicode.ttf
  Fuse = false
  Justification = 6
  JustificationReference = 0
  KeepLeftMargin = false
  MakeFace = true
  ObliqueAngle = 0
  Placement = pos=(64.9,-29.92,6.18) rot=(0,0,1;0rad)
  ScaleToSize = true
  Size = 3
  String = Entry
  Tracking = 0
FEATURE [Part::Part2DObjectPython] ShapeString003  label="ShapeStringMain"  # Draft 2D object (typed FeaturePython)
  FontFile = /Library/Fonts/Arial Unicode.ttf
  Fuse = false
  Justification = 6
  JustificationReference = 0
  KeepLeftMargin = false
  MakeFace = true
  ObliqueAngle = 0
  Placement = pos=(92.54,-30.76,6.18) rot=(0,0,1;0rad)
  ScaleToSize = true
  Size = 3
  String = Main
  Tracking = 0
FEATURE [Part::Part2DObjectPython] ShapeString004  label="ShapeStringPorch"  # Draft 2D object (typed FeaturePython)
  FontFile = /Library/Fonts/Arial Unicode.ttf
  Fuse = false
  Justification = 6
  JustificationReference = 0
  KeepLeftMargin = false
  MakeFace = true
  ObliqueAngle = 0
  Placement = pos=(9.18,-65.04,6.18) rot=(0,0,1;0rad)
  ScaleToSize = true
  Size = 3
  String = Porch
  Tracking = 0
FEATURE [Part::Part2DObjectPython] ShapeString005  label="ShapeStringTrailer"  # Draft 2D object (typed FeaturePython)
  FontFile = /Library/Fonts/Arial Unicode.ttf
  Fuse = false
  Justification = 6
  JustificationReference = 0
  KeepLeftMargin = false
  MakeFace = true
  ObliqueAngle = 0
  Placement = pos=(35.42,-65.01,6.18) rot=(0,0,1;0rad)
  ScaleToSize = true
  Size = 3
  String = Trailer
  Tracking = 0
FEATURE [Part::Part2DObjectPython] ShapeString006  label="ShapeStringWater"  # Draft 2D object (typed FeaturePython)
  FontFile = /Library/Fonts/Arial Unicode.ttf
  Fuse = false
  Justification = 6
  JustificationReference = 0
  KeepLeftMargin = false
  MakeFace = true
  ObliqueAngle = 0
  Placement = pos=(63.96,-64.76,6.18) rot=(0,0,1;0rad)
  ScaleToSize = true
  Size = 3
  String = Water
  Tracking = 0
FEATURE [Part::Part2DObjectPython] ShapeString007  label="ShapeStringPower"  # Draft 2D object (typed FeaturePython)
  FontFile = /Library/Fonts/Arial Unicode.ttf
  Fuse = false
  Justification = 6
  JustificationReference = 0
  KeepLeftMargin = false
  MakeFace = true
  ObliqueAngle = 0
  Placement = pos=(91.44,-64.52,6.18) rot=(0,0,1;0rad)
  ScaleToSize = true
  Size = 3
  String = Power
  Tracking = 0
FEATURE [PartDesign::Body] Body003  label="BodyFrontMountPcbButtonCover"
  AllowCompound = false
  Group = -> [Binder006,Sketch033,Pad024,Sketch034,Pad025,DatumPlane003,Mirrored004,Sketch040,Pad029,Pocket007,Sketch041,Pad030,Sketch042,Pad031,Sketch043,Pocket008,Binder007,Sketch048,Pad033,Sketch049,Pad034,DatumPlane,Mirrored,Sketch053,Pocket014,Sketch082,Pocket034,Fillet,Chamfer,ShapeString,ShapeString001,ShapeString002,ShapeString003,ShapeString004,ShapeString005,ShapeString006,ShapeString007]
  Origin = -> Origin013
  Tip = -> Chamfer
COMPONENT P10 — geometry summary ("trailer-switch-panel-eight-buttons-v003"; no construction recipe available for this part):
  bounding box: 113.4 x 65.8 x 9.1 mm
  tessellated surface: 20,717 triangles
  volume: 14121 mm^3 (21% of its bounding box)
PROVENANCE & LICENSES
A FreeCAD (.FCStd) document from a public repository crawl; recipes are the document's own serialized feature recipes (and, for linked parts, companion documents' recipes).
License: mit.
